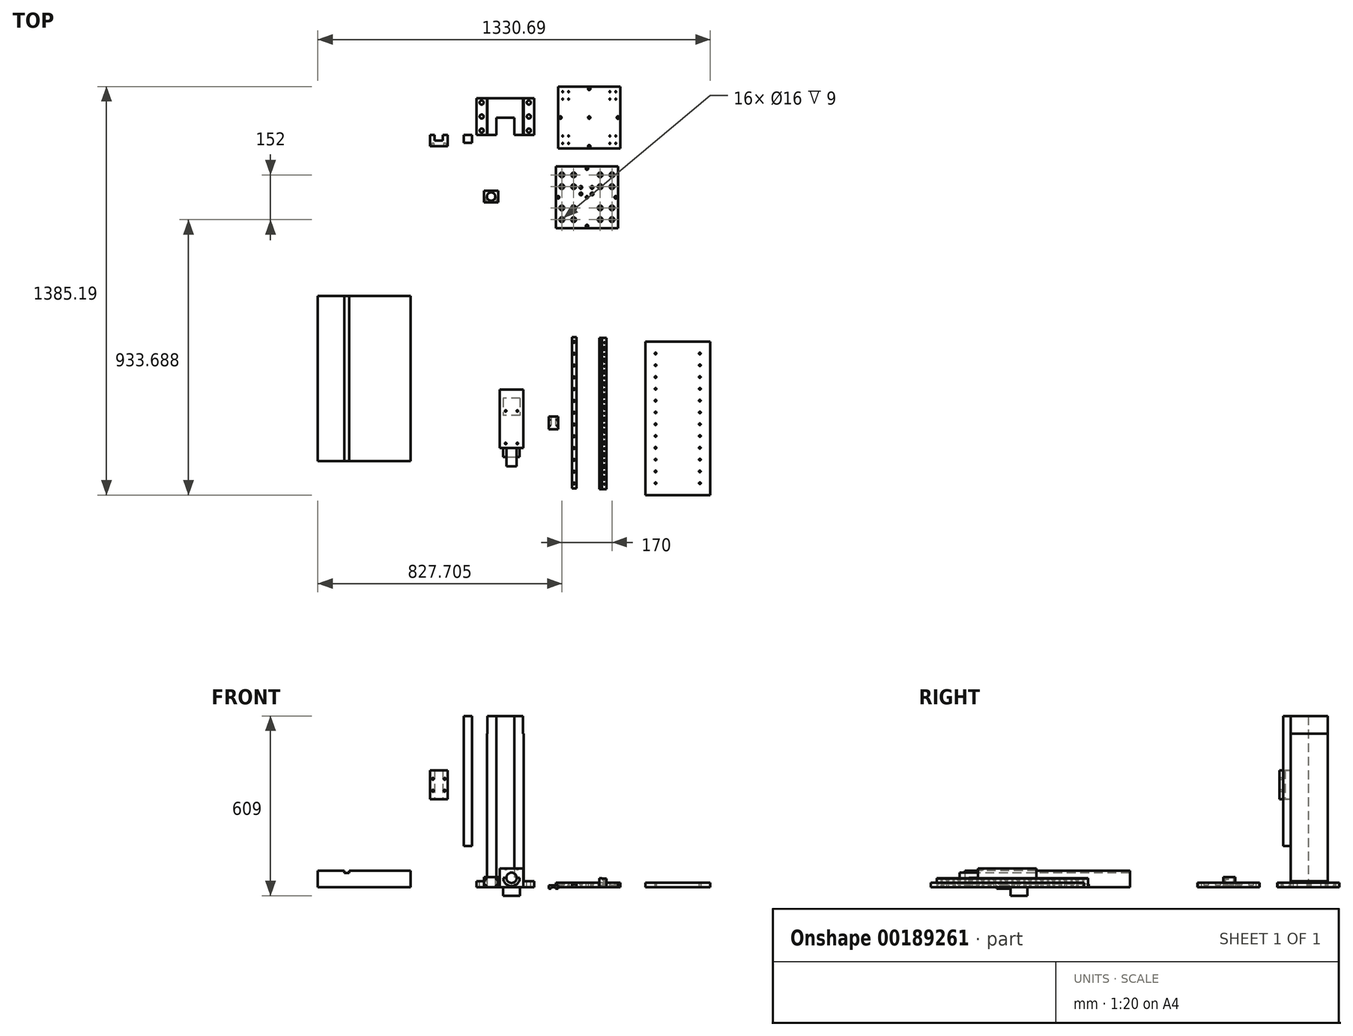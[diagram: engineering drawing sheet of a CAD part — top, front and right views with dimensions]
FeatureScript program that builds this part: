
annotation { "Feature Type Name" : "Feature", "Feature Type Description" : "" }
export const myFeature = defineFeature(function(context is Context, id is Id, definition is map)
    precondition{}
    {
        {
            var Q0;
            Q0=qCreatedBy(makeId("Top.planeOp"),FACE);
            var sketch = newSketch(context, id + "F0", { "sketchPlane" : qUnion([Q0])});
            skLineSegment(sketch, "E0.bottom", {"start": v(-121.15, 80.57) * mm, "end": v(3.85, 80.57) * mm});
            skLineSegment(sketch, "E0.top", {"start": v(-121.15, -44.43) * mm, "end": v(3.85, -44.43) * mm});
            skLineSegment(sketch, "E0.left", {"start": v(-121.15, 80.57) * mm, "end": v(-121.15, -44.43) * mm});
            skLineSegment(sketch, "E0.right", {"start": v(3.85, 80.57) * mm, "end": v(3.85, -44.43) * mm});
            skSolve(sketch);
        }
        {
            var Q0;
            Q0=makeQuery(id+"F0.imprint","IMPRINT",FACE,{"disambiguationData":[TD([[makeQuery(id+"F0.imprint","IMPRINT",EDGE,{"derivedFrom":sQuery(id+"F0.wireOp",EDGE,"E0.bottom")}),-1.0]])]});
            extrude(context, id + "F1", {"entities" : qUnion([Q0]), "depth" : 580 * mm});
        }
        {
            var Q0;
            Q0=makeQuery(id+"F1.opExtrude","SWEPT_FACE",FACE,{"disambiguationData":[OSD([sQuery(id+"F0.wireOp",EDGE,"E0.left")])]});
            var sketch = newSketch(context, id + "F2", { "sketchPlane" : qUnion([Q0])});
            skLineSegment(sketch, "E1.bottom", {"start": v(-80.57, 0) * mm, "end": v(44.43, 0) * mm});
            skLineSegment(sketch, "E1.top", {"start": v(-80.57, 20) * mm, "end": v(44.43, 20) * mm});
            skLineSegment(sketch, "E1.left", {"start": v(-80.57, 0) * mm, "end": v(-80.57, 20) * mm});
            skLineSegment(sketch, "E1.right", {"start": v(44.43, 0) * mm, "end": v(44.43, 20) * mm});
            skSolve(sketch);
        }
        {
            var Q0;
            Q0=makeQuery(id+"F2.imprint","IMPRINT",FACE,{"disambiguationData":[TD([[makeQuery(id+"F2.imprint","IMPRINT",EDGE,{"derivedFrom":sQuery(id+"F2.wireOp",EDGE,"E1.bottom")}),1.0]])]});
            extrude(context, id + "F3", {"entities" : qUnion([Q0]), "operationType" : NewBodyOperationType.ADD, "depth" : 35 * mm});
        }
        {
            var Q0;
            Q0=makeQuery(id+"F1.opExtrude","SWEPT_FACE",FACE,{"disambiguationData":[OSD([sQuery(id+"F0.wireOp",EDGE,"E0.right")])]});
            var sketch = newSketch(context, id + "F4", { "sketchPlane" : qUnion([Q0])});
            skLineSegment(sketch, "E2.bottom", {"start": v(-44.43, 0) * mm, "end": v(80.57, 0) * mm});
            skLineSegment(sketch, "E2.top", {"start": v(-44.43, 20) * mm, "end": v(80.57, 20) * mm});
            skLineSegment(sketch, "E2.left", {"start": v(-44.43, 0) * mm, "end": v(-44.43, 20) * mm});
            skLineSegment(sketch, "E2.right", {"start": v(80.57, 0) * mm, "end": v(80.57, 20) * mm});
            skSolve(sketch);
        }
        {
            var Q0;
            Q0=makeQuery(id+"F4.imprint","IMPRINT",FACE,{"disambiguationData":[TD([[makeQuery(id+"F4.imprint","IMPRINT",EDGE,{"derivedFrom":sQuery(id+"F4.wireOp",EDGE,"E2.bottom")}),-1.0]])]});
            extrude(context, id + "F5", {"entities" : qUnion([Q0]), "operationType" : NewBodyOperationType.ADD, "depth" : 35 * mm});
        }
        {
            var Q0;
            Q0=makeQuery(id+"F5.opExtrude","SWEPT_FACE",FACE,{"disambiguationData":[OSD([sQuery(id+"F4.wireOp",EDGE,"E2.top")])]});
            var sketch = newSketch(context, id + "F6", { "sketchPlane" : qUnion([Q0])});
            skCircle(sketch, "E3", {"center": v(21.35, 65.57) * mm, "radius": 7 * mm});
            skCircle(sketch, "E4", {"center": v(21.35, 18.07) * mm, "radius": 7 * mm});
            skCircle(sketch, "E5", {"center": v(21.35, -29.43) * mm, "radius": 7 * mm});
            skPoint(sketch, "E6", {"position": v(38.85, 18.07) * mm});
            skPoint(sketch, "E7", {"position": v(21.35, 80.57) * mm});
            skSolve(sketch);
        }
        {
            var Q0;
            Q0=makeQuery(id+"F6.imprint","IMPRINT",FACE,{"disambiguationData":[TD([[makeQuery(id+"F6.imprint","IMPRINT",EDGE,{"derivedFrom":sQuery(id+"F6.wireOp",EDGE,"E4")}),1.0]])]});
            var Q1;
            Q1=makeQuery(id+"F6.imprint","IMPRINT",FACE,{"disambiguationData":[TD([[makeQuery(id+"F6.imprint","IMPRINT",EDGE,{"derivedFrom":sQuery(id+"F6.wireOp",EDGE,"E5")}),1.0]])]});
            var Q2;
            Q2=makeQuery(id+"F6.imprint","IMPRINT",FACE,{"disambiguationData":[TD([[makeQuery(id+"F6.imprint","IMPRINT",EDGE,{"derivedFrom":sQuery(id+"F6.wireOp",EDGE,"E3")}),1.0]])]});
            extrude(context, id + "F7", {"entities" : qUnion([Q0, Q1, Q2]), "operationType" : NewBodyOperationType.REMOVE, "oppositeDirection" : true, "depth" : 20 * mm});
        }
        {
            var Q0;
            Q0=makeQuery(id+"F3.opExtrude","SWEPT_FACE",FACE,{"disambiguationData":[OSD([sQuery(id+"F2.wireOp",EDGE,"E1.top")])]});
            var sketch = newSketch(context, id + "F8", { "sketchPlane" : qUnion([Q0])});
            skPoint(sketch, "E8", {"position": v(-138.65, 80.57) * mm});
            skPoint(sketch, "E9", {"position": v(-156.15, 18.07) * mm});
            skCircle(sketch, "E10", {"center": v(-138.65, 65.57) * mm, "radius": 7 * mm});
            skCircle(sketch, "E11", {"center": v(-138.65, 18.07) * mm, "radius": 7 * mm});
            skCircle(sketch, "E12", {"center": v(-138.65, -29.43) * mm, "radius": 7 * mm});
            skSolve(sketch);
        }
        {
            var Q0;
            Q0=makeQuery(id+"F8.imprint","IMPRINT",FACE,{"disambiguationData":[TD([[makeQuery(id+"F8.imprint","IMPRINT",EDGE,{"derivedFrom":sQuery(id+"F8.wireOp",EDGE,"E10")}),1.0]])]});
            var Q1;
            Q1=makeQuery(id+"F8.imprint","IMPRINT",FACE,{"disambiguationData":[TD([[makeQuery(id+"F8.imprint","IMPRINT",EDGE,{"derivedFrom":sQuery(id+"F8.wireOp",EDGE,"E11")}),1.0]])]});
            var Q2;
            Q2=makeQuery(id+"F8.imprint","IMPRINT",FACE,{"disambiguationData":[TD([[makeQuery(id+"F8.imprint","IMPRINT",EDGE,{"derivedFrom":sQuery(id+"F8.wireOp",EDGE,"E12")}),1.0]])]});
            extrude(context, id + "F9", {"entities" : qUnion([Q0, Q1, Q2]), "operationType" : NewBodyOperationType.REMOVE, "oppositeDirection" : true, "depth" : 20 * mm});
        }
        {
            var Q0;
            {var subQ2=sQuery(id+"F2.wireOp",EDGE,"E1.top");Q0=makeQuery(id+"F2.imprint","IMPRINT",FACE,{"disambiguationData":[TD([[makeQuery(id+"F2.imprint","IMPRINT",EDGE,{"derivedFrom":subQ2}),1.0]])]});}
            var sketch = newSketch(context, id + "F10", { "sketchPlane" : qUnion([Q0])});
            skLineSegment(sketch, "E13.bottom", {"start": v(44.43, 580) * mm, "end": v(-80.57, 580) * mm});
            skLineSegment(sketch, "E13.top", {"start": v(44.43, 520) * mm, "end": v(-80.57, 520) * mm});
            skLineSegment(sketch, "E13.left", {"start": v(44.43, 580) * mm, "end": v(44.43, 520) * mm});
            skLineSegment(sketch, "E13.right", {"start": v(-80.57, 580) * mm, "end": v(-80.57, 520) * mm});
            skSolve(sketch);
        }
        {
            var Q0;
            Q0=makeQuery(id+"F10.imprint","IMPRINT",FACE,{"disambiguationData":[TD([[makeQuery(id+"F10.imprint","IMPRINT",EDGE,{"derivedFrom":sQuery(id+"F10.wireOp",EDGE,"E13.bottom")}),-1.0]])]});
            extrude(context, id + "F11", {"entities" : qUnion([Q0]), "operationType" : NewBodyOperationType.REMOVE, "oppositeDirection" : true, "depth" : 2 * mm});
        }
        {
            var Q0;
            {var subQ3=sQuery(id+"F4.wireOp",EDGE,"E2.top");Q0=makeQuery(id+"F4.imprint","IMPRINT",FACE,{"disambiguationData":[TD([[makeQuery(id+"F4.imprint","IMPRINT",EDGE,{"derivedFrom":subQ3}),1.0]])]});}
            var sketch = newSketch(context, id + "F12", { "sketchPlane" : qUnion([Q0])});
            skLineSegment(sketch, "E14.bottom", {"start": v(-44.43, 580) * mm, "end": v(80.57, 580) * mm});
            skLineSegment(sketch, "E14.top", {"start": v(-44.43, 520) * mm, "end": v(80.57, 520) * mm});
            skLineSegment(sketch, "E14.left", {"start": v(-44.43, 580) * mm, "end": v(-44.43, 520) * mm});
            skLineSegment(sketch, "E14.right", {"start": v(80.57, 580) * mm, "end": v(80.57, 520) * mm});
            skLineSegment(sketch, "E15", {"start": v(14.57, 580) * mm, "end": v(14.57, 50.87) * mm});
            skSolve(sketch);
        }
        {
            var Q0;
            Q0=makeQuery(id+"F12.imprint","IMPRINT",FACE,{"disambiguationData":[TD([[makeQuery(id+"F12.imprint","IMPRINT",EDGE,{"derivedFrom":sQuery(id+"F12.wireOp",EDGE,"E14.bottom")}),1.0]])]});
            extrude(context, id + "F13", {"entities" : qUnion([Q0]), "operationType" : NewBodyOperationType.REMOVE, "oppositeDirection" : true, "depth" : 2 * mm});
        }
        {
            var Q0;
            Q0=makeQuery(id+"F5.boolean.opBoolean","MERGE",FACE,{"derivedFrom":[makeQuery(id+"F3.boolean.opBoolean","MERGE",FACE,{"derivedFrom":[makeQuery(id+"F1.opExtrude","SWEPT_FACE",FACE,{"disambiguationData":[OSD([sQuery(id+"F0.wireOp",EDGE,"E0.top")])]}),makeQuery(id+"F3.opExtrude","SWEPT_FACE",FACE,{"disambiguationData":[OSD([sQuery(id+"F2.wireOp",EDGE,"E1.right")])]})]}),makeQuery(id+"F5.opExtrude","SWEPT_FACE",FACE,{"disambiguationData":[OSD([sQuery(id+"F4.wireOp",EDGE,"E2.left")])]})]});
            var sketch = newSketch(context, id + "F14", { "sketchPlane" : qUnion([Q0])});
            skPoint(sketch, "E16", {"position": v(-58.65, 580) * mm});
            skLineSegment(sketch, "E17.bottom", {"start": v(-88.9, 580) * mm, "end": v(-28.4, 580) * mm});
            skLineSegment(sketch, "E17.top", {"start": v(-88.9, 0) * mm, "end": v(-28.4, 0) * mm});
            skLineSegment(sketch, "E17.left", {"start": v(-88.9, 580) * mm, "end": v(-88.9, 0) * mm});
            skLineSegment(sketch, "E17.right", {"start": v(-28.4, 580) * mm, "end": v(-28.4, 0) * mm});
            skSolve(sketch);
        }
        {
            var Q0;
            Q0=makeQuery(id+"F14.imprint","IMPRINT",FACE,{"disambiguationData":[TD([[makeQuery(id+"F14.imprint","IMPRINT",EDGE,{"derivedFrom":sQuery(id+"F14.wireOp",EDGE,"E17.bottom")}),-1.0]])]});
            extrude(context, id + "F15", {"entities" : qUnion([Q0]), "operationType" : NewBodyOperationType.REMOVE, "oppositeDirection" : true, "depth" : 59 * mm});
        }
        {
            var Q0;
            Q0=makeQuery(id+"F5.boolean.opBoolean","MERGE",FACE,{"derivedFrom":[makeQuery(id+"F3.boolean.opBoolean","MERGE",FACE,{"derivedFrom":[makeQuery(id+"F1.opExtrude","SWEPT_FACE",FACE,{"disambiguationData":[OSD([sQuery(id+"F0.wireOp",EDGE,"E0.top")])]}),makeQuery(id+"F3.opExtrude","SWEPT_FACE",FACE,{"disambiguationData":[OSD([sQuery(id+"F2.wireOp",EDGE,"E1.right")])]})]}),makeQuery(id+"F5.opExtrude","SWEPT_FACE",FACE,{"disambiguationData":[OSD([sQuery(id+"F4.wireOp",EDGE,"E2.left")])]})]});
            var sketch = newSketch(context, id + "F16", { "sketchPlane" : qUnion([Q0])});
            skLineSegment(sketch, "E18.bottom", {"start": v(-199.32, 580) * mm, "end": v(-171.32, 580) * mm});
            skLineSegment(sketch, "E18.top", {"start": v(-199.32, 140) * mm, "end": v(-171.32, 140) * mm});
            skLineSegment(sketch, "E18.left", {"start": v(-199.32, 580) * mm, "end": v(-199.32, 140) * mm});
            skLineSegment(sketch, "E18.right", {"start": v(-171.32, 580) * mm, "end": v(-171.32, 140) * mm});
            skPoint(sketch, "E19", {"position": v(-185.32, 580) * mm});
            skPoint(sketch, "E20", {"position": v(-122.53, 0) * mm});
            skLineSegment(sketch, "E21.bottom", {"start": v(-314.15, 396.2) * mm, "end": v(-254.15, 396.2) * mm});
            skLineSegment(sketch, "E21.top", {"start": v(-314.15, 298.2) * mm, "end": v(-254.15, 298.2) * mm});
            skLineSegment(sketch, "E21.left", {"start": v(-314.15, 396.2) * mm, "end": v(-314.15, 298.2) * mm});
            skLineSegment(sketch, "E21.right", {"start": v(-254.15, 396.2) * mm, "end": v(-254.15, 298.2) * mm});
            skPoint(sketch, "E22", {"position": v(-284.15, 298.2) * mm});
            skSolve(sketch);
        }
        {
            var Q0;
            Q0=makeQuery(id+"F16.imprint","IMPRINT",FACE,{"disambiguationData":[TD([[makeQuery(id+"F16.imprint","IMPRINT",EDGE,{"derivedFrom":sQuery(id+"F16.wireOp",EDGE,"E18.bottom")}),-1.0]])]});
            extrude(context, id + "F17", {"entities" : qUnion([Q0]), "depth" : 26 * mm});
        }
        {
            var Q0;
            Q0=makeQuery(id+"F16.imprint","IMPRINT",FACE,{"disambiguationData":[TD([[makeQuery(id+"F16.imprint","IMPRINT",EDGE,{"derivedFrom":sQuery(id+"F16.wireOp",EDGE,"E21.bottom")}),-1.0]])]});
            extrude(context, id + "F18", {"entities" : qUnion([Q0]), "depth" : 38 * mm});
        }
        {
            var Q0;
            Q0=makeQuery(id+"F18.opExtrude","SWEPT_FACE",FACE,{"disambiguationData":[OSD([sQuery(id+"F16.wireOp",EDGE,"E21.top")])]});
            var sketch = newSketch(context, id + "F19", { "sketchPlane" : qUnion([Q0])});
            skLineSegment(sketch, "E23.bottom", {"start": v(-298.15, 44.43) * mm, "end": v(-270.15, 44.43) * mm});
            skLineSegment(sketch, "E23.top", {"start": v(-298.15, 63.43) * mm, "end": v(-270.15, 63.43) * mm});
            skLineSegment(sketch, "E23.left", {"start": v(-298.15, 44.43) * mm, "end": v(-298.15, 63.43) * mm});
            skLineSegment(sketch, "E23.right", {"start": v(-270.15, 44.43) * mm, "end": v(-270.15, 63.43) * mm});
            skPoint(sketch, "E24", {"position": v(-284.15, 44.43) * mm});
            skSolve(sketch);
        }
        {
            var Q0;
            Q0=makeQuery(id+"F19.imprint","IMPRINT",FACE,{"disambiguationData":[TD([[makeQuery(id+"F19.imprint","IMPRINT",EDGE,{"derivedFrom":sQuery(id+"F19.wireOp",EDGE,"E23.bottom")}),1.0]])]});
            extrude(context, id + "F20", {"entities" : qUnion([Q0]), "operationType" : NewBodyOperationType.REMOVE, "oppositeDirection" : true, "depth" : 98 * mm});
        }
        {
            var Q0;
            Q0=makeQuery(id+"F18.opExtrude","CAP_FACE",FACE,{"disambiguationData":[OSD([sQuery(id+"F16.wireOp",EDGE,"E21.bottom"),sQuery(id+"F16.wireOp",EDGE,"E21.top"),sQuery(id+"F16.wireOp",EDGE,"E21.left"),sQuery(id+"F16.wireOp",EDGE,"E21.right")])],"isStart":false});
            var sketch = newSketch(context, id + "F21", { "sketchPlane" : qUnion([Q0])});
            skCircle(sketch, "E25", {"center": v(-304.15, 367.2) * mm, "radius": 3.35 * mm});
            skCircle(sketch, "E26", {"center": v(-304.15, 327.2) * mm, "radius": 3.35 * mm});
            skCircle(sketch, "E27", {"center": v(-264.15, 367.2) * mm, "radius": 3.35 * mm});
            skCircle(sketch, "E28", {"center": v(-264.15, 327.2) * mm, "radius": 3.35 * mm});
            skPoint(sketch, "E29", {"position": v(-284.15, 396.2) * mm});
            skLineSegment(sketch, "E30", {"start": v(-284.15, 396.2) * mm, "end": v(-284.15, 298.2) * mm});
            skPoint(sketch, "E31", {"position": v(-284.15, 347.2) * mm});
            skSolve(sketch);
        }
        {
            var Q0;
            Q0=makeQuery(id+"F21.imprint","IMPRINT",FACE,{"disambiguationData":[TD([[makeQuery(id+"F21.imprint","IMPRINT",EDGE,{"derivedFrom":sQuery(id+"F21.wireOp",EDGE,"E25")}),1.0]])]});
            var Q1;
            Q1=makeQuery(id+"F21.imprint","IMPRINT",FACE,{"disambiguationData":[TD([[makeQuery(id+"F21.imprint","IMPRINT",EDGE,{"derivedFrom":sQuery(id+"F21.wireOp",EDGE,"E26")}),1.0]])]});
            var Q2;
            Q2=makeQuery(id+"F21.imprint","IMPRINT",FACE,{"disambiguationData":[TD([[makeQuery(id+"F21.imprint","IMPRINT",EDGE,{"derivedFrom":sQuery(id+"F21.wireOp",EDGE,"E27")}),1.0]])]});
            var Q3;
            Q3=makeQuery(id+"F21.imprint","IMPRINT",FACE,{"disambiguationData":[TD([[makeQuery(id+"F21.imprint","IMPRINT",EDGE,{"derivedFrom":sQuery(id+"F21.wireOp",EDGE,"E28")}),1.0]])]});
            extrude(context, id + "F22", {"entities" : qUnion([Q0, Q1, Q2, Q3]), "operationType" : NewBodyOperationType.REMOVE, "oppositeDirection" : true, "depth" : 10 * mm});
        }
        {
            var Q0;
            Q0=qCreatedBy(makeId("Top.planeOp"),FACE);
            var sketch = newSketch(context, id + "F23", { "sketchPlane" : qUnion([Q0])});
            skLineSegment(sketch, "E32.bottom", {"start": v(120.9, 119.72) * mm, "end": v(330.9, 119.72) * mm});
            skLineSegment(sketch, "E32.top", {"start": v(120.9, -90.28) * mm, "end": v(330.9, -90.28) * mm});
            skLineSegment(sketch, "E32.left", {"start": v(120.9, 119.72) * mm, "end": v(120.9, -90.28) * mm});
            skLineSegment(sketch, "E32.right", {"start": v(330.9, 119.72) * mm, "end": v(330.9, -90.28) * mm});
            skCircle(sketch, "E33", {"center": v(225.9, 14.72) * mm, "radius": 4 * mm});
            skCircle(sketch, "E34", {"center": v(323.4, 14.72) * mm, "radius": 4.2 * mm});
            skCircle(sketch, "E35", {"center": v(225.9, 112.22) * mm, "radius": 4.2 * mm});
            skCircle(sketch, "E36", {"center": v(128.4, 14.72) * mm, "radius": 4.2 * mm});
            skCircle(sketch, "E37", {"center": v(225.9, -82.78) * mm, "radius": 4.2 * mm});
            skLineSegment(sketch, "E38.bottom", {"start": v(113.2, -150.78) * mm, "end": v(323.2, -150.78) * mm});
            skLineSegment(sketch, "E38.top", {"start": v(113.2, -360.78) * mm, "end": v(323.2, -360.78) * mm});
            skLineSegment(sketch, "E38.left", {"start": v(113.2, -150.78) * mm, "end": v(113.2, -360.78) * mm});
            skLineSegment(sketch, "E38.right", {"start": v(323.2, -150.78) * mm, "end": v(323.2, -360.78) * mm});
            skCircle(sketch, "E39", {"center": v(218.2, -255.78) * mm, "radius": 4 * mm});
            skCircle(sketch, "E40", {"center": v(218.2, -158.28) * mm, "radius": 4.2 * mm});
            skCircle(sketch, "E41", {"center": v(120.7, -255.78) * mm, "radius": 4.2 * mm});
            skCircle(sketch, "E42", {"center": v(315.7, -255.78) * mm, "radius": 4.2 * mm});
            skCircle(sketch, "E43", {"center": v(218.2, -353.28) * mm, "radius": 4.2 * mm});
            skLineSegment(sketch, "E44.bottom", {"start": v(-694.5, -590.16) * mm, "end": v(-379.5, -590.16) * mm});
            skLineSegment(sketch, "E44.top", {"start": v(-694.5, -1150.16) * mm, "end": v(-379.5, -1150.16) * mm});
            skLineSegment(sketch, "E44.left", {"start": v(-694.5, -590.16) * mm, "end": v(-694.5, -1150.16) * mm});
            skLineSegment(sketch, "E44.right", {"start": v(-379.5, -590.16) * mm, "end": v(-379.5, -1150.16) * mm});
            skLineSegment(sketch, "E45.bottom", {"start": v(-130.67, -233.25) * mm, "end": v(-82.67, -233.25) * mm});
            skLineSegment(sketch, "E45.top", {"start": v(-130.67, -273.25) * mm, "end": v(-82.67, -273.25) * mm});
            skLineSegment(sketch, "E45.left", {"start": v(-130.67, -233.25) * mm, "end": v(-130.67, -273.25) * mm});
            skLineSegment(sketch, "E45.right", {"start": v(-82.67, -233.25) * mm, "end": v(-82.67, -273.25) * mm});
            skPoint(sketch, "E46", {"position": v(-106.67, -253.25) * mm});
            skCircle(sketch, "E47", {"center": v(-106.67, -253.25) * mm, "radius": 14 * mm});
            skCircle(sketch, "E48", {"center": v(303.2, -179.78) * mm, "radius": 4.5 * mm});
            skCircle(sketch, "E49", {"center": v(263.2, -179.78) * mm, "radius": 4.5 * mm});
            skCircle(sketch, "E50", {"center": v(263.2, -219.78) * mm, "radius": 4.5 * mm});
            skCircle(sketch, "E51", {"center": v(303.2, -219.78) * mm, "radius": 4.5 * mm});
            skCircle(sketch, "E52", {"center": v(303.2, -331.78) * mm, "radius": 4.5 * mm});
            skCircle(sketch, "E53", {"center": v(303.2, -291.78) * mm, "radius": 4.5 * mm});
            skCircle(sketch, "E54", {"center": v(263.2, -291.78) * mm, "radius": 4.5 * mm});
            skCircle(sketch, "E55", {"center": v(263.2, -331.78) * mm, "radius": 4.5 * mm});
            skCircle(sketch, "E56", {"center": v(173.2, -219.78) * mm, "radius": 4.5 * mm});
            skCircle(sketch, "E57", {"center": v(173.2, -179.78) * mm, "radius": 4.5 * mm});
            skCircle(sketch, "E58", {"center": v(133.2, -179.78) * mm, "radius": 4.5 * mm});
            skCircle(sketch, "E59", {"center": v(133.2, -219.78) * mm, "radius": 4.5 * mm});
            skCircle(sketch, "E60", {"center": v(173.2, -331.78) * mm, "radius": 4.5 * mm});
            skCircle(sketch, "E61", {"center": v(173.2, -291.78) * mm, "radius": 4.5 * mm});
            skCircle(sketch, "E62", {"center": v(133.2, -291.78) * mm, "radius": 4.5 * mm});
            skCircle(sketch, "E63", {"center": v(133.2, -331.78) * mm, "radius": 4.5 * mm});
            skCircle(sketch, "E64", {"center": v(263.2, -179.78) * mm, "radius": 8 * mm});
            skCircle(sketch, "E65", {"center": v(303.2, -179.78) * mm, "radius": 8 * mm});
            skCircle(sketch, "E66", {"center": v(263.2, -219.78) * mm, "radius": 8 * mm});
            skCircle(sketch, "E67", {"center": v(303.2, -219.78) * mm, "radius": 8 * mm});
            skCircle(sketch, "E68", {"center": v(263.2, -291.78) * mm, "radius": 8 * mm});
            skCircle(sketch, "E69", {"center": v(303.2, -291.78) * mm, "radius": 8 * mm});
            skCircle(sketch, "E70", {"center": v(263.2, -331.78) * mm, "radius": 8 * mm});
            skCircle(sketch, "E71", {"center": v(303.2, -331.78) * mm, "radius": 8 * mm});
            skCircle(sketch, "E72", {"center": v(173.2, -179.78) * mm, "radius": 8 * mm});
            skCircle(sketch, "E73", {"center": v(133.2, -179.78) * mm, "radius": 8 * mm});
            skCircle(sketch, "E74", {"center": v(133.2, -219.78) * mm, "radius": 8 * mm});
            skCircle(sketch, "E75", {"center": v(173.2, -219.78) * mm, "radius": 8 * mm});
            skCircle(sketch, "E76", {"center": v(133.2, -291.78) * mm, "radius": 8 * mm});
            skCircle(sketch, "E77", {"center": v(173.2, -291.78) * mm, "radius": 8 * mm});
            skCircle(sketch, "E78", {"center": v(133.2, -331.78) * mm, "radius": 8 * mm});
            skCircle(sketch, "E79", {"center": v(173.2, -331.78) * mm, "radius": 8 * mm});
            skCircle(sketch, "E80", {"center": v(197.7, -222.28) * mm, "radius": 2.65 * mm});
            skCircle(sketch, "E81", {"center": v(235.7, -222.28) * mm, "radius": 2.65 * mm});
            skCircle(sketch, "E82", {"center": v(197.7, -244.28) * mm, "radius": 2.65 * mm});
            skCircle(sketch, "E83", {"center": v(235.7, -244.28) * mm, "radius": 2.65 * mm});
            skCircle(sketch, "E84", {"center": v(197.7, -222.28) * mm, "radius": 4.75 * mm});
            skCircle(sketch, "E85", {"center": v(235.7, -222.28) * mm, "radius": 4.75 * mm});
            skCircle(sketch, "E86", {"center": v(197.7, -244.28) * mm, "radius": 4.75 * mm});
            skCircle(sketch, "E87", {"center": v(235.7, -244.28) * mm, "radius": 4.75 * mm});
            skLineSegment(sketch, "E88.bottom", {"start": v(-77.51, -907.41) * mm, "end": v(2.49, -907.41) * mm});
            skLineSegment(sketch, "E88.top", {"start": v(-77.51, -1105.61) * mm, "end": v(2.49, -1105.61) * mm});
            skLineSegment(sketch, "E88.left", {"start": v(-77.51, -907.41) * mm, "end": v(-77.51, -1105.61) * mm});
            skLineSegment(sketch, "E88.right", {"start": v(2.49, -907.41) * mm, "end": v(2.49, -1105.61) * mm});
            skCircle(sketch, "E89", {"center": v(-57.51, -1090.61) * mm, "radius": 2.68 * mm});
            skCircle(sketch, "E90", {"center": v(-17.51, -1090.61) * mm, "radius": 2.68 * mm});
            skCircle(sketch, "E91", {"center": v(-57.51, -980.61) * mm, "radius": 2.68 * mm});
            skCircle(sketch, "E92", {"center": v(-17.51, -980.61) * mm, "radius": 2.68 * mm});
            skLineSegment(sketch, "E93.bottom", {"start": v(88.31, -999.03) * mm, "end": v(120.31, -999.03) * mm});
            skLineSegment(sketch, "E93.top", {"start": v(88.31, -1042.03) * mm, "end": v(120.31, -1042.03) * mm});
            skLineSegment(sketch, "E93.left", {"start": v(88.31, -999.03) * mm, "end": v(88.31, -1042.03) * mm});
            skLineSegment(sketch, "E93.right", {"start": v(120.31, -999.03) * mm, "end": v(120.31, -1042.03) * mm});
            skLineSegment(sketch, "E94.bottom", {"start": v(167.32, -729.85) * mm, "end": v(182.32, -729.85) * mm});
            skLineSegment(sketch, "E94.top", {"start": v(167.32, -1242.85) * mm, "end": v(182.32, -1242.85) * mm});
            skLineSegment(sketch, "E94.left", {"start": v(167.32, -729.85) * mm, "end": v(167.32, -1242.85) * mm});
            skLineSegment(sketch, "E94.right", {"start": v(182.32, -729.85) * mm, "end": v(182.32, -1242.85) * mm});
            skCircle(sketch, "E95", {"center": v(174.82, -746.35) * mm, "radius": 1.75 * mm});
            skCircle(sketch, "E96", {"center": v(174.82, -786.35) * mm, "radius": 1.75 * mm});
            skCircle(sketch, "E97", {"center": v(174.82, -826.35) * mm, "radius": 1.75 * mm});
            skCircle(sketch, "E98", {"center": v(174.82, -866.35) * mm, "radius": 1.75 * mm});
            skCircle(sketch, "E99", {"center": v(174.82, -906.35) * mm, "radius": 1.75 * mm});
            skCircle(sketch, "E100", {"center": v(174.82, -946.35) * mm, "radius": 1.75 * mm});
            skCircle(sketch, "E101", {"center": v(174.82, -986.35) * mm, "radius": 1.75 * mm});
            skCircle(sketch, "E102", {"center": v(174.82, -1026.35) * mm, "radius": 1.75 * mm});
            skCircle(sketch, "E103", {"center": v(174.82, -1066.35) * mm, "radius": 1.75 * mm});
            skCircle(sketch, "E104", {"center": v(174.82, -1106.35) * mm, "radius": 1.75 * mm});
            skCircle(sketch, "E105", {"center": v(174.82, -1146.35) * mm, "radius": 1.75 * mm});
            skCircle(sketch, "E106", {"center": v(174.82, -1186.35) * mm, "radius": 1.75 * mm});
            skCircle(sketch, "E107", {"center": v(174.82, -1226.35) * mm, "radius": 1.75 * mm});
            skPoint(sketch, "E108", {"position": v(174.82, -729.85) * mm});
            skPoint(sketch, "E109", {"position": v(277.23, -732.27) * mm});
            skLineSegment(sketch, "E110.right", {"start": v(284.73, -732.27) * mm, "end": v(284.73, -1245.27) * mm});
            skLineSegment(sketch, "E110.left", {"start": v(269.73, -732.27) * mm, "end": v(269.73, -1245.27) * mm});
            skCircle(sketch, "E111", {"center": v(277.23, -948.77) * mm, "radius": 1.75 * mm});
            skCircle(sketch, "E112", {"center": v(277.23, -1228.77) * mm, "radius": 1.75 * mm});
            skCircle(sketch, "E113", {"center": v(277.23, -1068.77) * mm, "radius": 1.75 * mm});
            skCircle(sketch, "E114", {"center": v(277.23, -1108.77) * mm, "radius": 1.75 * mm});
            skCircle(sketch, "E115", {"center": v(277.23, -1148.77) * mm, "radius": 1.75 * mm});
            skCircle(sketch, "E116", {"center": v(277.23, -988.77) * mm, "radius": 1.75 * mm});
            skCircle(sketch, "E117", {"center": v(277.23, -908.77) * mm, "radius": 1.75 * mm});
            skCircle(sketch, "E118", {"center": v(277.23, -788.77) * mm, "radius": 1.75 * mm});
            skLineSegment(sketch, "E110.top", {"start": v(269.73, -1245.27) * mm, "end": v(284.73, -1245.27) * mm});
            skCircle(sketch, "E119", {"center": v(277.23, -868.77) * mm, "radius": 1.75 * mm});
            skCircle(sketch, "E120", {"center": v(277.23, -1188.77) * mm, "radius": 1.75 * mm});
            skCircle(sketch, "E121", {"center": v(277.23, -1028.77) * mm, "radius": 1.75 * mm});
            skCircle(sketch, "E122", {"center": v(277.23, -748.77) * mm, "radius": 1.75 * mm});
            skCircle(sketch, "E123", {"center": v(277.23, -828.77) * mm, "radius": 1.75 * mm});
            skLineSegment(sketch, "E110.bottom", {"start": v(269.73, -732.27) * mm, "end": v(284.73, -732.27) * mm});
            skLineSegment(sketch, "E124.bottom", {"start": v(269.73, -732.27) * mm, "end": v(260.23, -732.27) * mm});
            skLineSegment(sketch, "E124.top", {"start": v(269.73, -1245.27) * mm, "end": v(260.23, -1245.27) * mm});
            skLineSegment(sketch, "E124.right", {"start": v(260.23, -732.27) * mm, "end": v(260.23, -1245.27) * mm});
            skCircle(sketch, "E125", {"center": v(277.23, -1208.77) * mm, "radius": 2.8 * mm});
            skCircle(sketch, "E126", {"center": v(277.23, -1168.77) * mm, "radius": 2.8 * mm});
            skCircle(sketch, "E127", {"center": v(277.23, -1128.77) * mm, "radius": 2.8 * mm});
            skCircle(sketch, "E128", {"center": v(277.23, -1088.77) * mm, "radius": 2.8 * mm});
            skCircle(sketch, "E129", {"center": v(277.23, -1048.77) * mm, "radius": 2.8 * mm});
            skCircle(sketch, "E130", {"center": v(277.23, -1008.77) * mm, "radius": 2.8 * mm});
            skCircle(sketch, "E131", {"center": v(277.23, -968.77) * mm, "radius": 2.8 * mm});
            skCircle(sketch, "E132", {"center": v(277.23, -928.77) * mm, "radius": 2.8 * mm});
            skCircle(sketch, "E133", {"center": v(277.23, -888.77) * mm, "radius": 2.8 * mm});
            skCircle(sketch, "E134", {"center": v(277.23, -848.77) * mm, "radius": 2.8 * mm});
            skCircle(sketch, "E135", {"center": v(277.23, -808.77) * mm, "radius": 2.8 * mm});
            skCircle(sketch, "E136", {"center": v(277.23, -768.77) * mm, "radius": 2.8 * mm});
            skLineSegment(sketch, "E137.bottom", {"start": v(416.18, -745.47) * mm, "end": v(636.18, -745.47) * mm});
            skLineSegment(sketch, "E137.top", {"start": v(416.18, -1265.47) * mm, "end": v(636.18, -1265.47) * mm});
            skLineSegment(sketch, "E137.left", {"start": v(416.18, -745.47) * mm, "end": v(416.18, -1265.47) * mm});
            skLineSegment(sketch, "E137.right", {"start": v(636.18, -745.47) * mm, "end": v(636.18, -1265.47) * mm});
            skCircle(sketch, "E138", {"center": v(451.18, -905.47) * mm, "radius": 2.8 * mm});
            skCircle(sketch, "E139", {"center": v(451.18, -865.47) * mm, "radius": 2.8 * mm});
            skCircle(sketch, "E140", {"center": v(451.18, -825.47) * mm, "radius": 2.8 * mm});
            skCircle(sketch, "E141", {"center": v(451.18, -785.47) * mm, "radius": 2.8 * mm});
            skCircle(sketch, "E142", {"center": v(451.18, -1065.47) * mm, "radius": 2.8 * mm});
            skCircle(sketch, "E143", {"center": v(451.18, -1105.47) * mm, "radius": 2.8 * mm});
            skCircle(sketch, "E144", {"center": v(451.18, -1145.47) * mm, "radius": 2.8 * mm});
            skCircle(sketch, "E145", {"center": v(451.18, -1185.47) * mm, "radius": 2.8 * mm});
            skCircle(sketch, "E146", {"center": v(451.18, -1225.47) * mm, "radius": 2.8 * mm});
            skCircle(sketch, "E147", {"center": v(451.18, -945.47) * mm, "radius": 2.8 * mm});
            skCircle(sketch, "E148", {"center": v(451.18, -985.47) * mm, "radius": 2.8 * mm});
            skCircle(sketch, "E149", {"center": v(451.18, -1025.47) * mm, "radius": 2.8 * mm});
            skCircle(sketch, "E150", {"center": v(601.18, -905.47) * mm, "radius": 2.8 * mm});
            skCircle(sketch, "E151", {"center": v(601.18, -865.47) * mm, "radius": 2.8 * mm});
            skCircle(sketch, "E152", {"center": v(601.18, -825.47) * mm, "radius": 2.8 * mm});
            skCircle(sketch, "E153", {"center": v(601.18, -785.47) * mm, "radius": 2.8 * mm});
            skCircle(sketch, "E154", {"center": v(601.18, -1065.47) * mm, "radius": 2.8 * mm});
            skCircle(sketch, "E155", {"center": v(601.18, -1105.47) * mm, "radius": 2.8 * mm});
            skCircle(sketch, "E156", {"center": v(601.18, -1145.47) * mm, "radius": 2.8 * mm});
            skCircle(sketch, "E157", {"center": v(601.18, -1185.47) * mm, "radius": 2.8 * mm});
            skCircle(sketch, "E158", {"center": v(601.18, -1225.47) * mm, "radius": 2.8 * mm});
            skCircle(sketch, "E159", {"center": v(601.18, -945.47) * mm, "radius": 2.8 * mm});
            skCircle(sketch, "E160", {"center": v(601.18, -985.47) * mm, "radius": 2.8 * mm});
            skCircle(sketch, "E161", {"center": v(601.18, -1025.47) * mm, "radius": 2.8 * mm});
            skPoint(sketch, "E162", {"position": v(526.18, -745.47) * mm});
            skCircle(sketch, "E163", {"center": v(135.9, 102.22) * mm, "radius": 1.6 * mm});
            skCircle(sketch, "E164", {"center": v(155.9, 102.22) * mm, "radius": 1.6 * mm});
            skCircle(sketch, "E165", {"center": v(135.9, 77.22) * mm, "radius": 1.6 * mm});
            skCircle(sketch, "E166", {"center": v(155.9, 77.22) * mm, "radius": 1.6 * mm});
            skCircle(sketch, "E167", {"center": v(155.9, 102.22) * mm, "radius": 3 * mm});
            skCircle(sketch, "E168", {"center": v(155.9, 77.22) * mm, "radius": 3 * mm});
            skCircle(sketch, "E169", {"center": v(135.9, 102.22) * mm, "radius": 3 * mm});
            skCircle(sketch, "E170", {"center": v(135.9, 77.22) * mm, "radius": 3 * mm});
            skCircle(sketch, "E171.1.0.0", {"center": v(295.9, 77.22) * mm, "radius": 1.6 * mm});
            skCircle(sketch, "E171.1.0.1", {"center": v(295.9, 102.22) * mm, "radius": 1.6 * mm});
            skCircle(sketch, "E171.1.0.2", {"center": v(295.9, 77.22) * mm, "radius": 3 * mm});
            skCircle(sketch, "E171.1.0.3", {"center": v(315.9, 102.22) * mm, "radius": 1.6 * mm});
            skCircle(sketch, "E171.1.0.4", {"center": v(315.9, 77.22) * mm, "radius": 3 * mm});
            skCircle(sketch, "E171.1.0.5", {"center": v(315.9, 77.22) * mm, "radius": 1.6 * mm});
            skCircle(sketch, "E171.1.0.6", {"center": v(315.9, 102.22) * mm, "radius": 3 * mm});
            skCircle(sketch, "E171.1.0.7", {"center": v(295.9, 102.22) * mm, "radius": 3 * mm});
            skLineSegment(sketch, "E171.direction1", {"start": v(155.9, 77.22) * mm, "end": v(315.9, 77.22) * mm, "construction": true});
            skLineSegment(sketch, "E172.1.0.0", {"start": v(155.9, -72.78) * mm, "end": v(315.9, -72.78) * mm, "construction": true});
            skCircle(sketch, "E172.1.0.1", {"center": v(135.9, -47.78) * mm, "radius": 1.6 * mm});
            skCircle(sketch, "E172.1.0.2", {"center": v(155.9, -47.78) * mm, "radius": 1.6 * mm});
            skCircle(sketch, "E172.1.0.3", {"center": v(315.9, -47.78) * mm, "radius": 3 * mm});
            skCircle(sketch, "E172.1.0.4", {"center": v(295.9, -72.78) * mm, "radius": 3 * mm});
            skCircle(sketch, "E172.1.0.5", {"center": v(295.9, -72.78) * mm, "radius": 1.6 * mm});
            skCircle(sketch, "E172.1.0.6", {"center": v(135.9, -72.78) * mm, "radius": 3 * mm});
            skCircle(sketch, "E172.1.0.7", {"center": v(315.9, -47.78) * mm, "radius": 1.6 * mm});
            skCircle(sketch, "E172.1.0.8", {"center": v(135.9, -47.78) * mm, "radius": 3 * mm});
            skCircle(sketch, "E172.1.0.9", {"center": v(135.9, -72.78) * mm, "radius": 1.6 * mm});
            skCircle(sketch, "E172.1.0.10", {"center": v(155.9, -47.78) * mm, "radius": 3 * mm});
            skCircle(sketch, "E172.1.0.11", {"center": v(315.9, -72.78) * mm, "radius": 3 * mm});
            skCircle(sketch, "E172.1.0.12", {"center": v(295.9, -47.78) * mm, "radius": 3 * mm});
            skCircle(sketch, "E172.1.0.13", {"center": v(295.9, -47.78) * mm, "radius": 1.6 * mm});
            skCircle(sketch, "E172.1.0.14", {"center": v(155.9, -72.78) * mm, "radius": 1.6 * mm});
            skCircle(sketch, "E172.1.0.15", {"center": v(315.9, -72.78) * mm, "radius": 1.6 * mm});
            skCircle(sketch, "E172.1.0.16", {"center": v(155.9, -72.78) * mm, "radius": 3 * mm});
            skLineSegment(sketch, "E172.direction1", {"start": v(155.9, 77.22) * mm, "end": v(155.9, -72.78) * mm, "construction": true});
            skSolve(sketch);
        }
        {
            var Q0;
            Q0=makeQuery(id+"F23.imprint","IMPRINT",FACE,{"disambiguationData":[TD([[makeQuery(id+"F23.imprint","IMPRINT",EDGE,{"derivedFrom":sQuery(id+"F23.wireOp",EDGE,"E32.bottom")}),-1.0]])]});
            extrude(context, id + "F24", {"entities" : qUnion([Q0]), "depth" : 15 * mm});
        }
        {
            var Q0;
            Q0=makeQuery(id+"F23.imprint","IMPRINT",FACE,{"disambiguationData":[TD([[makeQuery(id+"F23.imprint","IMPRINT",EDGE,{"derivedFrom":sQuery(id+"F23.wireOp",EDGE,"E38.bottom")}),-1.0]])]});
            extrude(context, id + "F25", {"entities" : qUnion([Q0]), "depth" : 15 * mm});
        }
        {
            var Q0;
            Q0=makeQuery(id+"F23.imprint","IMPRINT",FACE,{"disambiguationData":[TD([[makeQuery(id+"F23.imprint","IMPRINT",EDGE,{"derivedFrom":sQuery(id+"F23.wireOp",EDGE,"E44.bottom")}),-1.0]])]});
            extrude(context, id + "F27", {"entities" : qUnion([Q0]), "depth" : 55 * mm});
        }
        {
            var Q0;
            Q0=makeQuery(id+"F23.imprint","IMPRINT",FACE,{"disambiguationData":[TD([[makeQuery(id+"F23.imprint","IMPRINT",EDGE,{"derivedFrom":sQuery(id+"F23.wireOp",EDGE,"E45.bottom")}),-1.0]])]});
            extrude(context, id + "F28", {"entities" : qUnion([Q0]), "depth" : 34 * mm});
        }
        {
            var Q0;
            Q0=makeQuery(id+"F27.opExtrude","SWEPT_FACE",FACE,{"disambiguationData":[OSD([sQuery(id+"F23.wireOp",EDGE,"E44.top")])]});
            var sketch = newSketch(context, id + "F29", { "sketchPlane" : qUnion([Q0])});
            skLineSegment(sketch, "E173.bottom", {"start": v(-604.5, 55) * mm, "end": v(-588.5, 55) * mm});
            skLineSegment(sketch, "E173.top", {"start": v(-604.5, 47.5) * mm, "end": v(-588.5, 47.5) * mm});
            skLineSegment(sketch, "E173.left", {"start": v(-604.5, 55) * mm, "end": v(-604.5, 47.5) * mm});
            skLineSegment(sketch, "E173.right", {"start": v(-588.5, 55) * mm, "end": v(-588.5, 47.5) * mm});
            skSolve(sketch);
        }
        {
            var Q0;
            Q0=makeQuery(id+"F29.imprint","IMPRINT",FACE,{"disambiguationData":[TD([[makeQuery(id+"F29.imprint","IMPRINT",EDGE,{"derivedFrom":sQuery(id+"F29.wireOp",EDGE,"E173.bottom")}),-1.0]])]});
            extrude(context, id + "F30", {"entities" : qUnion([Q0]), "operationType" : NewBodyOperationType.REMOVE, "oppositeDirection" : true, "depth" : 560 * mm});
        }
        {
            var Q0;
            Q0=makeQuery(id+"F23.imprint","IMPRINT",FACE,{"disambiguationData":[TD([[makeQuery(id+"F23.imprint","IMPRINT",EDGE,{"derivedFrom":sQuery(id+"F23.wireOp",EDGE,"E55")}),-1.0]])]});
            var Q1;
            Q1=makeQuery(id+"F23.imprint","IMPRINT",FACE,{"disambiguationData":[TD([[makeQuery(id+"F23.imprint","IMPRINT",EDGE,{"derivedFrom":sQuery(id+"F23.wireOp",EDGE,"E54")}),-1.0]])]});
            var Q2;
            Q2=makeQuery(id+"F23.imprint","IMPRINT",FACE,{"disambiguationData":[TD([[makeQuery(id+"F23.imprint","IMPRINT",EDGE,{"derivedFrom":sQuery(id+"F23.wireOp",EDGE,"E53")}),-1.0]])]});
            var Q3;
            Q3=makeQuery(id+"F23.imprint","IMPRINT",FACE,{"disambiguationData":[TD([[makeQuery(id+"F23.imprint","IMPRINT",EDGE,{"derivedFrom":sQuery(id+"F23.wireOp",EDGE,"E52")}),-1.0]])]});
            var Q4;
            Q4=makeQuery(id+"F23.imprint","IMPRINT",FACE,{"disambiguationData":[TD([[makeQuery(id+"F23.imprint","IMPRINT",EDGE,{"derivedFrom":sQuery(id+"F23.wireOp",EDGE,"E50")}),-1.0]])]});
            var Q5;
            Q5=makeQuery(id+"F23.imprint","IMPRINT",FACE,{"disambiguationData":[TD([[makeQuery(id+"F23.imprint","IMPRINT",EDGE,{"derivedFrom":sQuery(id+"F23.wireOp",EDGE,"E51")}),-1.0]])]});
            var Q6;
            Q6=makeQuery(id+"F23.imprint","IMPRINT",FACE,{"disambiguationData":[TD([[makeQuery(id+"F23.imprint","IMPRINT",EDGE,{"derivedFrom":sQuery(id+"F23.wireOp",EDGE,"E49")}),-1.0]])]});
            var Q7;
            Q7=makeQuery(id+"F23.imprint","IMPRINT",FACE,{"disambiguationData":[TD([[makeQuery(id+"F23.imprint","IMPRINT",EDGE,{"derivedFrom":sQuery(id+"F23.wireOp",EDGE,"E48")}),-1.0]])]});
            var Q8;
            Q8=makeQuery(id+"F23.imprint","IMPRINT",FACE,{"disambiguationData":[TD([[makeQuery(id+"F23.imprint","IMPRINT",EDGE,{"derivedFrom":sQuery(id+"F23.wireOp",EDGE,"E58")}),-1.0]])]});
            var Q9;
            Q9=makeQuery(id+"F23.imprint","IMPRINT",FACE,{"disambiguationData":[TD([[makeQuery(id+"F23.imprint","IMPRINT",EDGE,{"derivedFrom":sQuery(id+"F23.wireOp",EDGE,"E57")}),-1.0]])]});
            var Q10;
            Q10=makeQuery(id+"F23.imprint","IMPRINT",FACE,{"disambiguationData":[TD([[makeQuery(id+"F23.imprint","IMPRINT",EDGE,{"derivedFrom":sQuery(id+"F23.wireOp",EDGE,"E59")}),-1.0]])]});
            var Q11;
            Q11=makeQuery(id+"F23.imprint","IMPRINT",FACE,{"disambiguationData":[TD([[makeQuery(id+"F23.imprint","IMPRINT",EDGE,{"derivedFrom":sQuery(id+"F23.wireOp",EDGE,"E56")}),-1.0]])]});
            var Q12;
            Q12=makeQuery(id+"F23.imprint","IMPRINT",FACE,{"disambiguationData":[TD([[makeQuery(id+"F23.imprint","IMPRINT",EDGE,{"derivedFrom":sQuery(id+"F23.wireOp",EDGE,"E62")}),-1.0]])]});
            var Q13;
            Q13=makeQuery(id+"F23.imprint","IMPRINT",FACE,{"disambiguationData":[TD([[makeQuery(id+"F23.imprint","IMPRINT",EDGE,{"derivedFrom":sQuery(id+"F23.wireOp",EDGE,"E61")}),-1.0]])]});
            var Q14;
            Q14=makeQuery(id+"F23.imprint","IMPRINT",FACE,{"disambiguationData":[TD([[makeQuery(id+"F23.imprint","IMPRINT",EDGE,{"derivedFrom":sQuery(id+"F23.wireOp",EDGE,"E63")}),-1.0]])]});
            var Q15;
            Q15=makeQuery(id+"F23.imprint","IMPRINT",FACE,{"disambiguationData":[TD([[makeQuery(id+"F23.imprint","IMPRINT",EDGE,{"derivedFrom":sQuery(id+"F23.wireOp",EDGE,"E60")}),-1.0]])]});
            var Q16;
            Q16=sQuery(id+"F23.wireOp",EDGE,"E70");
            var Q17;
            Q17=sQuery(id+"F23.wireOp",EDGE,"E71");
            var Q18;
            Q18=sQuery(id+"F23.wireOp",EDGE,"E68");
            var Q19;
            Q19=sQuery(id+"F23.wireOp",EDGE,"E69");
            var Q20;
            Q20=sQuery(id+"F23.wireOp",EDGE,"E66");
            var Q21;
            Q21=sQuery(id+"F23.wireOp",EDGE,"E67");
            var Q22;
            Q22=sQuery(id+"F23.wireOp",EDGE,"E64");
            var Q23;
            Q23=sQuery(id+"F23.wireOp",EDGE,"E65");
            extrude(context, id + "F31", {"entities" : qUnion([Q0, Q1, Q2, Q3, Q4, Q5, Q6, Q7, Q8, Q9, Q10, Q11, Q12, Q13, Q14, Q15]), "operationType" : NewBodyOperationType.ADD, "surfaceEntities" : qUnion([Q16, Q17, Q18, Q19, Q20, Q21, Q22, Q23]), "depth" : 6 * mm});
        }
        {
            var Q0;
            Q0=makeQuery(id+"F28.opExtrude","SWEPT_FACE",FACE,{"disambiguationData":[OSD([sQuery(id+"F23.wireOp",EDGE,"E45.top")])]});
            var sketch = newSketch(context, id + "F32", { "sketchPlane" : qUnion([Q0])});
            skCircle(sketch, "E174", {"center": v(-125.67, 27.5) * mm, "radius": 2.02 * mm});
            skCircle(sketch, "E175", {"center": v(-87.67, 27.5) * mm, "radius": 2.02 * mm});
            skCircle(sketch, "E176", {"center": v(-125.67, 5.5) * mm, "radius": 2.02 * mm});
            skCircle(sketch, "E177", {"center": v(-87.67, 5.5) * mm, "radius": 2.02 * mm});
            skSolve(sketch);
        }
        {
            var Q0;
            Q0=makeQuery(id+"F32.imprint","IMPRINT",FACE,{"disambiguationData":[TD([[makeQuery(id+"F32.imprint","IMPRINT",EDGE,{"derivedFrom":sQuery(id+"F32.wireOp",EDGE,"E174")}),1.0]])]});
            var Q1;
            Q1=makeQuery(id+"F32.imprint","IMPRINT",FACE,{"disambiguationData":[TD([[makeQuery(id+"F32.imprint","IMPRINT",EDGE,{"derivedFrom":sQuery(id+"F32.wireOp",EDGE,"E176")}),1.0]])]});
            var Q2;
            Q2=makeQuery(id+"F32.imprint","IMPRINT",FACE,{"disambiguationData":[TD([[makeQuery(id+"F32.imprint","IMPRINT",EDGE,{"derivedFrom":sQuery(id+"F32.wireOp",EDGE,"E177")}),1.0]])]});
            var Q3;
            Q3=makeQuery(id+"F32.imprint","IMPRINT",FACE,{"disambiguationData":[TD([[makeQuery(id+"F32.imprint","IMPRINT",EDGE,{"derivedFrom":sQuery(id+"F32.wireOp",EDGE,"E175")}),1.0]])]});
            extrude(context, id + "F33", {"entities" : qUnion([Q0, Q1, Q2, Q3]), "operationType" : NewBodyOperationType.REMOVE, "oppositeDirection" : true, "depth" : 17 * mm});
        }
        {
            var Q0;
            Q0=makeQuery(id+"F23.imprint","IMPRINT",FACE,{"disambiguationData":[TD([[makeQuery(id+"F23.imprint","IMPRINT",EDGE,{"derivedFrom":sQuery(id+"F23.wireOp",EDGE,"E80")}),-1.0]])]});
            var Q1;
            Q1=makeQuery(id+"F23.imprint","IMPRINT",FACE,{"disambiguationData":[TD([[makeQuery(id+"F23.imprint","IMPRINT",EDGE,{"derivedFrom":sQuery(id+"F23.wireOp",EDGE,"E82")}),-1.0]])]});
            var Q2;
            Q2=makeQuery(id+"F23.imprint","IMPRINT",FACE,{"disambiguationData":[TD([[makeQuery(id+"F23.imprint","IMPRINT",EDGE,{"derivedFrom":sQuery(id+"F23.wireOp",EDGE,"E81")}),-1.0]])]});
            var Q3;
            Q3=makeQuery(id+"F23.imprint","IMPRINT",FACE,{"disambiguationData":[TD([[makeQuery(id+"F23.imprint","IMPRINT",EDGE,{"derivedFrom":sQuery(id+"F23.wireOp",EDGE,"E83")}),-1.0]])]});
            extrude(context, id + "F34", {"entities" : qUnion([Q0, Q1, Q2, Q3]), "operationType" : NewBodyOperationType.ADD, "depth" : 8 * mm});
        }
        {
            var Q0;
            Q0=makeQuery(id+"F23.imprint","IMPRINT",FACE,{"disambiguationData":[TD([[makeQuery(id+"F23.imprint","IMPRINT",EDGE,{"derivedFrom":sQuery(id+"F23.wireOp",EDGE,"E88.bottom")}),-1.0]])]});
            extrude(context, id + "F35", {"entities" : qUnion([Q0]), "depth" : 63 * mm});
        }
        {
            var Q0;
            Q0=makeQuery(id+"F23.imprint","IMPRINT",FACE,{"disambiguationData":[TD([[makeQuery(id+"F23.imprint","IMPRINT",EDGE,{"derivedFrom":sQuery(id+"F23.wireOp",EDGE,"E90")}),1.0]])]});
            var Q1;
            Q1=makeQuery(id+"F23.imprint","IMPRINT",FACE,{"disambiguationData":[TD([[makeQuery(id+"F23.imprint","IMPRINT",EDGE,{"derivedFrom":sQuery(id+"F23.wireOp",EDGE,"E89")}),1.0]])]});
            var Q2;
            Q2=makeQuery(id+"F23.imprint","IMPRINT",FACE,{"disambiguationData":[TD([[makeQuery(id+"F23.imprint","IMPRINT",EDGE,{"derivedFrom":sQuery(id+"F23.wireOp",EDGE,"E92")}),1.0]])]});
            var Q3;
            Q3=makeQuery(id+"F23.imprint","IMPRINT",FACE,{"disambiguationData":[TD([[makeQuery(id+"F23.imprint","IMPRINT",EDGE,{"derivedFrom":sQuery(id+"F23.wireOp",EDGE,"E91")}),1.0]])]});
            extrude(context, id + "F36", {"entities" : qUnion([Q0, Q1, Q2, Q3]), "operationType" : NewBodyOperationType.ADD, "depth" : 58 * mm});
        }
        {
            var Q0;
            Q0=makeQuery(id+"F23.imprint","IMPRINT",FACE,{"disambiguationData":[TD([[makeQuery(id+"F23.imprint","IMPRINT",EDGE,{"derivedFrom":sQuery(id+"F23.wireOp",EDGE,"E88.bottom")}),-1.0]])]});
            var sketch = newSketch(context, id + "F37", { "sketchPlane" : qUnion([Q0])});
            skLineSegment(sketch, "E178.bottom", {"start": v(-8.76, -937.61) * mm, "end": v(-66.26, -937.61) * mm});
            skLineSegment(sketch, "E178.top", {"start": v(-8.76, -995.11) * mm, "end": v(-66.26, -995.11) * mm});
            skLineSegment(sketch, "E178.left", {"start": v(-8.76, -937.61) * mm, "end": v(-8.76, -995.11) * mm});
            skLineSegment(sketch, "E178.right", {"start": v(-66.26, -937.61) * mm, "end": v(-66.26, -995.11) * mm});
            skSolve(sketch);
        }
        {
            var Q0;
            Q0=makeQuery(id+"F37.imprint","IMPRINT",FACE,{"disambiguationData":[TD([[makeQuery(id+"F37.imprint","IMPRINT",EDGE,{"derivedFrom":sQuery(id+"F37.wireOp",EDGE,"E178.bottom")}),1.0]])]});
            extrude(context, id + "F38", {"entities" : qUnion([Q0]), "operationType" : NewBodyOperationType.ADD, "oppositeDirection" : true, "depth" : 29 * mm});
        }
        {
            var Q0;
            Q0=makeQuery(id+"F23.imprint","IMPRINT",FACE,{"disambiguationData":[TD([[makeQuery(id+"F23.imprint","IMPRINT",EDGE,{"derivedFrom":sQuery(id+"F23.wireOp",EDGE,"E91")}),1.0]])]});
            var Q1;
            Q1=makeQuery(id+"F23.imprint","IMPRINT",FACE,{"disambiguationData":[TD([[makeQuery(id+"F23.imprint","IMPRINT",EDGE,{"derivedFrom":sQuery(id+"F23.wireOp",EDGE,"E92")}),1.0]])]});
            extrude(context, id + "F39", {"entities" : qUnion([Q0, Q1]), "operationType" : NewBodyOperationType.ADD, "oppositeDirection" : true, "depth" : 29 * mm});
        }
        {
            var Q0;
            Q0=makeQuery(id+"F35.opExtrude","SWEPT_FACE",FACE,{"disambiguationData":[OSD([sQuery(id+"F23.wireOp",EDGE,"E88.top")])]});
            var sketch = newSketch(context, id + "F40", { "sketchPlane" : qUnion([Q0])});
            skCircle(sketch, "E179", {"center": v(-37.51, 31.5) * mm, "radius": 28 * mm});
            skPoint(sketch, "E180", {"position": v(-77.51, 31.5) * mm});
            skPoint(sketch, "E181", {"position": v(-37.51, 63) * mm});
            skLineSegment(sketch, "E182", {"start": v(-77.51, 31.5) * mm, "end": v(2.49, 31.5) * mm});
            skLineSegment(sketch, "E183", {"start": v(-37.51, 63) * mm, "end": v(-37.51, 0) * mm});
            skCircle(sketch, "E184", {"center": v(-37.51, 31.5) * mm, "radius": 17.5 * mm});
            skSolve(sketch);
        }
        {
            var Q0;
            {var subQ0=sQuery(id+"F40.wireOp",EDGE,"E184");var subQ3=sQuery(id+"F40.wireOp",EDGE,"E182");var subQ4=makeQuery(id+"F40.imprint","INTERSECT",VERTEX,{"disambiguationData":[OD(0.0)],"derivedFrom":[subQ3,subQ0]});Q0=makeQuery(id+"F40.imprint","IMPRINT",FACE,{"disambiguationData":[TD([[makeQuery(id+"F40.imprint","IMPRINT",EDGE,{"disambiguationData":[TD([[subQ4,-1.0]])],"derivedFrom":subQ3}),1.0]])]});}
            var Q1;
            {var subQ1=sQuery(id+"F40.wireOp",EDGE,"E183");var subQ3=sQuery(id+"F40.wireOp",EDGE,"E182");var subQ5=makeQuery(id+"F40.imprint","INTERSECT",VERTEX,{"derivedFrom":[subQ3,subQ1]});Q1=makeQuery(id+"F40.imprint","IMPRINT",FACE,{"disambiguationData":[TD([[makeQuery(id+"F40.imprint","IMPRINT",EDGE,{"disambiguationData":[TD([[subQ5,-1.0]])],"derivedFrom":subQ3}),1.0]])]});}
            var Q2;
            {var subQ0=sQuery(id+"F40.wireOp",EDGE,"E184");var subQ3=sQuery(id+"F40.wireOp",EDGE,"E182");var subQ4=makeQuery(id+"F40.imprint","INTERSECT",VERTEX,{"disambiguationData":[OD(0.0)],"derivedFrom":[subQ3,subQ0]});Q2=makeQuery(id+"F40.imprint","IMPRINT",FACE,{"disambiguationData":[TD([[makeQuery(id+"F40.imprint","IMPRINT",EDGE,{"disambiguationData":[TD([[subQ4,-1.0]])],"derivedFrom":subQ3}),-1.0]])]});}
            var Q3;
            {var subQ0=sQuery(id+"F40.wireOp",EDGE,"E183");var subQ3=sQuery(id+"F40.wireOp",EDGE,"E182");var subQ4=makeQuery(id+"F40.imprint","INTERSECT",VERTEX,{"derivedFrom":[subQ3,subQ0]});Q3=makeQuery(id+"F40.imprint","IMPRINT",FACE,{"disambiguationData":[TD([[makeQuery(id+"F40.imprint","IMPRINT",EDGE,{"disambiguationData":[TD([[subQ4,-1.0]])],"derivedFrom":subQ3}),-1.0]])]});}
            extrude(context, id + "F41", {"entities" : qUnion([Q0, Q1, Q2, Q3]), "operationType" : NewBodyOperationType.ADD, "depth" : 62.5 * mm});
        }
        {
            var Q0;
            {var subQ3=sQuery(id+"F40.wireOp",EDGE,"E182");var subQ5=sQuery(id+"F40.wireOp",EDGE,"E179");var subQ7=makeQuery(id+"F40.imprint","INTERSECT",VERTEX,{"disambiguationData":[OD(1.0)],"derivedFrom":[subQ5,subQ3]});Q0=makeQuery(id+"F40.imprint","IMPRINT",FACE,{"disambiguationData":[TD([[makeQuery(id+"F40.imprint","IMPRINT",EDGE,{"disambiguationData":[TD([[subQ7,-1.0]])],"derivedFrom":subQ5}),1.0]])]});}
            var Q1;
            {var subQ0=sQuery(id+"F40.wireOp",EDGE,"E183");var subQ3=sQuery(id+"F40.wireOp",EDGE,"E179");var subQ4=makeQuery(id+"F40.imprint","INTERSECT",VERTEX,{"disambiguationData":[OD(0.0)],"derivedFrom":[subQ3,subQ0]});Q1=makeQuery(id+"F40.imprint","IMPRINT",FACE,{"disambiguationData":[TD([[makeQuery(id+"F40.imprint","IMPRINT",EDGE,{"disambiguationData":[TD([[subQ4,-1.0]])],"derivedFrom":subQ3}),1.0]])]});}
            var Q2;
            {var subQ1=sQuery(id+"F40.wireOp",EDGE,"E183");var subQ5=sQuery(id+"F40.wireOp",EDGE,"E179");var subQ6=makeQuery(id+"F40.imprint","INTERSECT",VERTEX,{"disambiguationData":[OD(0.0)],"derivedFrom":[subQ5,subQ1]});Q2=makeQuery(id+"F40.imprint","IMPRINT",FACE,{"disambiguationData":[TD([[makeQuery(id+"F40.imprint","IMPRINT",EDGE,{"disambiguationData":[TD([[subQ6,1.0]])],"derivedFrom":subQ5}),1.0]])]});}
            var Q3;
            {var subQ3=sQuery(id+"F40.wireOp",EDGE,"E182");var subQ5=sQuery(id+"F40.wireOp",EDGE,"E179");var subQ7=makeQuery(id+"F40.imprint","INTERSECT",VERTEX,{"disambiguationData":[OD(0.0)],"derivedFrom":[subQ5,subQ3]});Q3=makeQuery(id+"F40.imprint","IMPRINT",FACE,{"disambiguationData":[TD([[makeQuery(id+"F40.imprint","IMPRINT",EDGE,{"disambiguationData":[TD([[subQ7,1.0]])],"derivedFrom":subQ5}),1.0]])]});}
            extrude(context, id + "F42", {"entities" : qUnion([Q0, Q1, Q2, Q3]), "operationType" : NewBodyOperationType.ADD, "depth" : 30.5 * mm});
        }
        {
            var Q0;
            Q0=makeQuery(id+"F23.imprint","IMPRINT",FACE,{"disambiguationData":[TD([[makeQuery(id+"F23.imprint","IMPRINT",EDGE,{"derivedFrom":sQuery(id+"F23.wireOp",EDGE,"E93.bottom")}),-1.0]])]});
            extrude(context, id + "F43", {"entities" : qUnion([Q0]), "depth" : 6.5 * mm});
        }
        {
            var Q0;
            Q0=makeQuery(id+"F23.imprint","IMPRINT",FACE,{"disambiguationData":[TD([[makeQuery(id+"F23.imprint","IMPRINT",EDGE,{"derivedFrom":sQuery(id+"F23.wireOp",EDGE,"E93.bottom")}),-1.0]])]});
            var sketch = newSketch(context, id + "F44", { "sketchPlane" : qUnion([Q0])});
            skLineSegment(sketch, "E185.bottom", {"start": v(120.31, -999.03) * mm, "end": v(111.81, -999.03) * mm});
            skLineSegment(sketch, "E185.top", {"start": v(120.31, -1042.03) * mm, "end": v(111.81, -1042.03) * mm});
            skLineSegment(sketch, "E185.left", {"start": v(120.31, -999.03) * mm, "end": v(120.31, -1042.03) * mm});
            skLineSegment(sketch, "E185.right", {"start": v(111.81, -999.03) * mm, "end": v(111.81, -1042.03) * mm});
            skLineSegment(sketch, "E186.bottom", {"start": v(96.81, -999.03) * mm, "end": v(88.31, -999.03) * mm});
            skLineSegment(sketch, "E186.top", {"start": v(96.81, -1042.03) * mm, "end": v(88.31, -1042.03) * mm});
            skLineSegment(sketch, "E186.left", {"start": v(96.81, -999.03) * mm, "end": v(96.81, -1042.03) * mm});
            skLineSegment(sketch, "E186.right", {"start": v(88.31, -999.03) * mm, "end": v(88.31, -1042.03) * mm});
            skSolve(sketch);
        }
        {
            var Q0;
            Q0=qSketchRegion(id+"F44",true);
            extrude(context, id + "F45", {"entities" : qUnion([Q0]), "operationType" : NewBodyOperationType.ADD, "oppositeDirection" : true, "depth" : 5.5 * mm});
        }
        {
            var Q0;
            Q0=makeQuery(id+"F43.opExtrude","CAP_FACE",FACE,{"disambiguationData":[OSD([sQuery(id+"F23.wireOp",EDGE,"E93.bottom"),sQuery(id+"F23.wireOp",EDGE,"E93.top"),sQuery(id+"F23.wireOp",EDGE,"E93.left"),sQuery(id+"F23.wireOp",EDGE,"E93.right")])],"isStart":false});
            var sketch = newSketch(context, id + "F46", { "sketchPlane" : qUnion([Q0])});
            skCircle(sketch, "E187", {"center": v(91.81, -1010.53) * mm, "radius": 1.34 * mm});
            skCircle(sketch, "E188", {"center": v(116.81, -1010.53) * mm, "radius": 1.34 * mm});
            skCircle(sketch, "E189", {"center": v(91.81, -1030.53) * mm, "radius": 1.34 * mm});
            skCircle(sketch, "E190", {"center": v(116.81, -1030.53) * mm, "radius": 1.34 * mm});
            skSolve(sketch);
        }
        {
            var Q0;
            Q0=makeQuery(id+"F46.imprint","IMPRINT",FACE,{"disambiguationData":[TD([[makeQuery(id+"F46.imprint","IMPRINT",EDGE,{"derivedFrom":sQuery(id+"F46.wireOp",EDGE,"E189")}),1.0]])]});
            var Q1;
            Q1=makeQuery(id+"F46.imprint","IMPRINT",FACE,{"disambiguationData":[TD([[makeQuery(id+"F46.imprint","IMPRINT",EDGE,{"derivedFrom":sQuery(id+"F46.wireOp",EDGE,"E187")}),1.0]])]});
            var Q2;
            Q2=makeQuery(id+"F46.imprint","IMPRINT",FACE,{"disambiguationData":[TD([[makeQuery(id+"F46.imprint","IMPRINT",EDGE,{"derivedFrom":sQuery(id+"F46.wireOp",EDGE,"E188")}),1.0]])]});
            var Q3;
            Q3=makeQuery(id+"F46.imprint","IMPRINT",FACE,{"disambiguationData":[TD([[makeQuery(id+"F46.imprint","IMPRINT",EDGE,{"derivedFrom":sQuery(id+"F46.wireOp",EDGE,"E190")}),1.0]])]});
            var Q4;
            Q4=sQuery(id+"F46.wireOp",EDGE,"E187");
            var Q5;
            Q5=sQuery(id+"F46.wireOp",EDGE,"E189");
            var Q6;
            Q6=sQuery(id+"F46.wireOp",EDGE,"E190");
            var Q7;
            Q7=sQuery(id+"F46.wireOp",EDGE,"E188");
            extrude(context, id + "F47", {"entities" : qUnion([Q0, Q1, Q2, Q3]), "operationType" : NewBodyOperationType.REMOVE, "surfaceEntities" : qUnion([Q4, Q5, Q6, Q7]), "oppositeDirection" : true, "depth" : 4 * mm});
        }
        {
            var Q0;
            Q0=makeQuery(id+"F23.imprint","IMPRINT",FACE,{"disambiguationData":[TD([[makeQuery(id+"F23.imprint","IMPRINT",EDGE,{"derivedFrom":sQuery(id+"F23.wireOp",EDGE,"E94.bottom")}),-1.0]])]});
            extrude(context, id + "F48", {"entities" : qUnion([Q0]), "depth" : 9.5 * mm});
        }
        {
            var Q0;
            Q0=makeQuery(id+"F48.opExtrude","CAP_FACE",FACE,{"disambiguationData":[OSD([sQuery(id+"F23.wireOp",EDGE,"E94.bottom"),sQuery(id+"F23.wireOp",EDGE,"E94.top"),sQuery(id+"F23.wireOp",EDGE,"E94.left"),sQuery(id+"F23.wireOp",EDGE,"E94.right"),sQuery(id+"F23.wireOp",EDGE,"E95"),sQuery(id+"F23.wireOp",EDGE,"E96"),sQuery(id+"F23.wireOp",EDGE,"E97"),sQuery(id+"F23.wireOp",EDGE,"E98"),sQuery(id+"F23.wireOp",EDGE,"E99"),sQuery(id+"F23.wireOp",EDGE,"E100"),sQuery(id+"F23.wireOp",EDGE,"E101"),sQuery(id+"F23.wireOp",EDGE,"E102"),sQuery(id+"F23.wireOp",EDGE,"E103"),sQuery(id+"F23.wireOp",EDGE,"E104"),sQuery(id+"F23.wireOp",EDGE,"E105"),sQuery(id+"F23.wireOp",EDGE,"E106"),sQuery(id+"F23.wireOp",EDGE,"E107")])],"isStart":false});
            var sketch = newSketch(context, id + "F49", { "sketchPlane" : qUnion([Q0])});
            skCircle(sketch, "E191", {"center": v(174.82, -746.35) * mm, "radius": 3 * mm});
            skCircle(sketch, "E192", {"center": v(174.82, -786.35) * mm, "radius": 3 * mm});
            skCircle(sketch, "E193", {"center": v(174.82, -826.35) * mm, "radius": 3 * mm});
            skCircle(sketch, "E194", {"center": v(174.82, -866.35) * mm, "radius": 3 * mm});
            skCircle(sketch, "E195", {"center": v(174.82, -906.35) * mm, "radius": 3 * mm});
            skCircle(sketch, "E196", {"center": v(174.82, -946.35) * mm, "radius": 3 * mm});
            skCircle(sketch, "E197", {"center": v(174.82, -986.35) * mm, "radius": 3 * mm});
            skCircle(sketch, "E198", {"center": v(174.82, -1026.35) * mm, "radius": 3 * mm});
            skCircle(sketch, "E199", {"center": v(174.82, -1066.35) * mm, "radius": 3 * mm});
            skCircle(sketch, "E200", {"center": v(174.82, -1106.35) * mm, "radius": 3 * mm});
            skCircle(sketch, "E201", {"center": v(174.82, -1146.35) * mm, "radius": 3 * mm});
            skCircle(sketch, "E202", {"center": v(174.82, -1186.35) * mm, "radius": 3 * mm});
            skCircle(sketch, "E203", {"center": v(174.82, -1226.35) * mm, "radius": 3 * mm});
            skSolve(sketch);
        }
        {
            var Q0;
            Q0=makeQuery(id+"F49.imprint","IMPRINT",FACE,{"disambiguationData":[TD([[makeQuery(id+"F49.imprint","IMPRINT",EDGE,{"derivedFrom":sQuery(id+"F49.wireOp",EDGE,"E191")}),1.0]])]});
            var Q1;
            Q1=makeQuery(id+"F49.imprint","IMPRINT",FACE,{"disambiguationData":[TD([[makeQuery(id+"F49.imprint","IMPRINT",EDGE,{"derivedFrom":sQuery(id+"F49.wireOp",EDGE,"E192")}),1.0]])]});
            var Q2;
            Q2=makeQuery(id+"F49.imprint","IMPRINT",FACE,{"disambiguationData":[TD([[makeQuery(id+"F49.imprint","IMPRINT",EDGE,{"derivedFrom":sQuery(id+"F49.wireOp",EDGE,"E193")}),1.0]])]});
            var Q3;
            Q3=makeQuery(id+"F49.imprint","IMPRINT",FACE,{"disambiguationData":[TD([[makeQuery(id+"F49.imprint","IMPRINT",EDGE,{"derivedFrom":sQuery(id+"F49.wireOp",EDGE,"E194")}),1.0]])]});
            var Q4;
            Q4=makeQuery(id+"F49.imprint","IMPRINT",FACE,{"disambiguationData":[TD([[makeQuery(id+"F49.imprint","IMPRINT",EDGE,{"derivedFrom":sQuery(id+"F49.wireOp",EDGE,"E195")}),1.0]])]});
            var Q5;
            Q5=makeQuery(id+"F49.imprint","IMPRINT",FACE,{"disambiguationData":[TD([[makeQuery(id+"F49.imprint","IMPRINT",EDGE,{"derivedFrom":sQuery(id+"F49.wireOp",EDGE,"E196")}),1.0]])]});
            var Q6;
            Q6=makeQuery(id+"F49.imprint","IMPRINT",FACE,{"disambiguationData":[TD([[makeQuery(id+"F49.imprint","IMPRINT",EDGE,{"derivedFrom":sQuery(id+"F49.wireOp",EDGE,"E197")}),1.0]])]});
            var Q7;
            Q7=makeQuery(id+"F49.imprint","IMPRINT",FACE,{"disambiguationData":[TD([[makeQuery(id+"F49.imprint","IMPRINT",EDGE,{"derivedFrom":sQuery(id+"F49.wireOp",EDGE,"E198")}),1.0]])]});
            var Q8;
            Q8=makeQuery(id+"F49.imprint","IMPRINT",FACE,{"disambiguationData":[TD([[makeQuery(id+"F49.imprint","IMPRINT",EDGE,{"derivedFrom":sQuery(id+"F49.wireOp",EDGE,"E199")}),1.0]])]});
            var Q9;
            Q9=makeQuery(id+"F49.imprint","IMPRINT",FACE,{"disambiguationData":[TD([[makeQuery(id+"F49.imprint","IMPRINT",EDGE,{"derivedFrom":sQuery(id+"F49.wireOp",EDGE,"E200")}),1.0]])]});
            var Q10;
            Q10=makeQuery(id+"F49.imprint","IMPRINT",FACE,{"disambiguationData":[TD([[makeQuery(id+"F49.imprint","IMPRINT",EDGE,{"derivedFrom":sQuery(id+"F49.wireOp",EDGE,"E201")}),1.0]])]});
            var Q11;
            Q11=makeQuery(id+"F49.imprint","IMPRINT",FACE,{"disambiguationData":[TD([[makeQuery(id+"F49.imprint","IMPRINT",EDGE,{"derivedFrom":sQuery(id+"F49.wireOp",EDGE,"E202")}),1.0]])]});
            var Q12;
            Q12=makeQuery(id+"F49.imprint","IMPRINT",FACE,{"disambiguationData":[TD([[makeQuery(id+"F49.imprint","IMPRINT",EDGE,{"derivedFrom":sQuery(id+"F49.wireOp",EDGE,"E203")}),1.0]])]});
            var Q13;
            Q13=sQuery(id+"F49.wireOp",EDGE,"E191");
            var Q14;
            Q14=sQuery(id+"F49.wireOp",EDGE,"E192");
            var Q15;
            Q15=sQuery(id+"F49.wireOp",EDGE,"E193");
            var Q16;
            Q16=sQuery(id+"F49.wireOp",EDGE,"E194");
            var Q17;
            Q17=sQuery(id+"F49.wireOp",EDGE,"E195");
            var Q18;
            Q18=sQuery(id+"F49.wireOp",EDGE,"E196");
            var Q19;
            Q19=sQuery(id+"F49.wireOp",EDGE,"E197");
            var Q20;
            Q20=sQuery(id+"F49.wireOp",EDGE,"E198");
            var Q21;
            Q21=sQuery(id+"F49.wireOp",EDGE,"E199");
            var Q22;
            Q22=sQuery(id+"F49.wireOp",EDGE,"E200");
            var Q23;
            Q23=sQuery(id+"F49.wireOp",EDGE,"E201");
            var Q24;
            Q24=sQuery(id+"F49.wireOp",EDGE,"E202");
            var Q25;
            Q25=sQuery(id+"F49.wireOp",EDGE,"E203");
            extrude(context, id + "F50", {"entities" : qUnion([Q0, Q1, Q2, Q3, Q4, Q5, Q6, Q7, Q8, Q9, Q10, Q11, Q12]), "operationType" : NewBodyOperationType.REMOVE, "surfaceEntities" : qUnion([Q13, Q14, Q15, Q16, Q17, Q18, Q19, Q20, Q21, Q22, Q23, Q24, Q25]), "oppositeDirection" : true, "depth" : 4.7 * mm});
        }
        {
            var Q0;
            Q0=makeQuery(id+"F23.imprint","IMPRINT",FACE,{"disambiguationData":[TD([[makeQuery(id+"F23.imprint","IMPRINT",EDGE,{"derivedFrom":sQuery(id+"F23.wireOp",EDGE,"E124.bottom")}),1.0]])]});
            extrude(context, id + "F51", {"entities" : qUnion([Q0]), "depth" : 30 * mm});
        }
        {
            var Q0;
            Q0=makeQuery(id+"F23.imprint","IMPRINT",FACE,{"disambiguationData":[TD([[makeQuery(id+"F23.imprint","IMPRINT",EDGE,{"derivedFrom":sQuery(id+"F23.wireOp",EDGE,"E110.right")}),-1.0]])]});
            extrude(context, id + "F52", {"entities" : qUnion([Q0]), "operationType" : NewBodyOperationType.ADD, "depth" : 29 * mm});
        }
        {
            var Q0;
            Q0=makeQuery(id+"F52.opExtrude","CAP_FACE",FACE,{"disambiguationData":[OSD([sQuery(id+"F23.wireOp",EDGE,"E110.right"),sQuery(id+"F23.wireOp",EDGE,"E111"),sQuery(id+"F23.wireOp",EDGE,"E112"),sQuery(id+"F23.wireOp",EDGE,"E113"),sQuery(id+"F23.wireOp",EDGE,"E114"),sQuery(id+"F23.wireOp",EDGE,"E115"),sQuery(id+"F23.wireOp",EDGE,"E116"),sQuery(id+"F23.wireOp",EDGE,"E117"),sQuery(id+"F23.wireOp",EDGE,"E118"),sQuery(id+"F23.wireOp",EDGE,"E110.top"),sQuery(id+"F23.wireOp",EDGE,"E119"),sQuery(id+"F23.wireOp",EDGE,"E120"),sQuery(id+"F23.wireOp",EDGE,"E121"),sQuery(id+"F23.wireOp",EDGE,"E122"),sQuery(id+"F23.wireOp",EDGE,"E123"),sQuery(id+"F23.wireOp",EDGE,"E110.bottom"),sQuery(id+"F23.wireOp",EDGE,"E110.left"),sQuery(id+"F23.wireOp",EDGE,"E125"),sQuery(id+"F23.wireOp",EDGE,"E126"),sQuery(id+"F23.wireOp",EDGE,"E127"),sQuery(id+"F23.wireOp",EDGE,"E128"),sQuery(id+"F23.wireOp",EDGE,"E129"),sQuery(id+"F23.wireOp",EDGE,"E130"),sQuery(id+"F23.wireOp",EDGE,"E131"),sQuery(id+"F23.wireOp",EDGE,"E132"),sQuery(id+"F23.wireOp",EDGE,"E133"),sQuery(id+"F23.wireOp",EDGE,"E134"),sQuery(id+"F23.wireOp",EDGE,"E135"),sQuery(id+"F23.wireOp",EDGE,"E136")])],"isStart":false});
            var sketch = newSketch(context, id + "F53", { "sketchPlane" : qUnion([Q0])});
            skCircle(sketch, "E204", {"center": v(277.23, -768.77) * mm, "radius": 5 * mm});
            skCircle(sketch, "E205", {"center": v(277.23, -808.77) * mm, "radius": 5 * mm});
            skCircle(sketch, "E206", {"center": v(277.23, -848.77) * mm, "radius": 5 * mm});
            skCircle(sketch, "E207", {"center": v(277.23, -888.77) * mm, "radius": 5 * mm});
            skCircle(sketch, "E208", {"center": v(277.23, -928.77) * mm, "radius": 5 * mm});
            skCircle(sketch, "E209", {"center": v(277.23, -968.77) * mm, "radius": 5 * mm});
            skCircle(sketch, "E210", {"center": v(277.23, -1008.77) * mm, "radius": 5 * mm});
            skCircle(sketch, "E211", {"center": v(277.23, -1048.77) * mm, "radius": 5 * mm});
            skCircle(sketch, "E212", {"center": v(277.23, -1088.77) * mm, "radius": 5 * mm});
            skCircle(sketch, "E213", {"center": v(277.23, -1128.77) * mm, "radius": 5 * mm});
            skCircle(sketch, "E214", {"center": v(277.23, -1168.77) * mm, "radius": 5 * mm});
            skCircle(sketch, "E215", {"center": v(277.23, -1208.77) * mm, "radius": 5 * mm});
            skSolve(sketch);
        }
        {
            var Q0;
            Q0=makeQuery(id+"F53.imprint","IMPRINT",FACE,{"disambiguationData":[TD([[makeQuery(id+"F53.imprint","IMPRINT",EDGE,{"derivedFrom":sQuery(id+"F53.wireOp",EDGE,"E204")}),1.0]])]});
            var Q1;
            Q1=makeQuery(id+"F53.imprint","IMPRINT",FACE,{"disambiguationData":[TD([[makeQuery(id+"F53.imprint","IMPRINT",EDGE,{"derivedFrom":sQuery(id+"F53.wireOp",EDGE,"E205")}),1.0]])]});
            var Q2;
            Q2=makeQuery(id+"F53.imprint","IMPRINT",FACE,{"disambiguationData":[TD([[makeQuery(id+"F53.imprint","IMPRINT",EDGE,{"derivedFrom":sQuery(id+"F53.wireOp",EDGE,"E206")}),1.0]])]});
            var Q3;
            Q3=makeQuery(id+"F53.imprint","IMPRINT",FACE,{"disambiguationData":[TD([[makeQuery(id+"F53.imprint","IMPRINT",EDGE,{"derivedFrom":sQuery(id+"F53.wireOp",EDGE,"E207")}),1.0]])]});
            var Q4;
            Q4=makeQuery(id+"F53.imprint","IMPRINT",FACE,{"disambiguationData":[TD([[makeQuery(id+"F53.imprint","IMPRINT",EDGE,{"derivedFrom":sQuery(id+"F53.wireOp",EDGE,"E208")}),1.0]])]});
            var Q5;
            Q5=makeQuery(id+"F53.imprint","IMPRINT",FACE,{"disambiguationData":[TD([[makeQuery(id+"F53.imprint","IMPRINT",EDGE,{"derivedFrom":sQuery(id+"F53.wireOp",EDGE,"E209")}),1.0]])]});
            var Q6;
            Q6=makeQuery(id+"F53.imprint","IMPRINT",FACE,{"disambiguationData":[TD([[makeQuery(id+"F53.imprint","IMPRINT",EDGE,{"derivedFrom":sQuery(id+"F53.wireOp",EDGE,"E210")}),1.0]])]});
            var Q7;
            Q7=makeQuery(id+"F53.imprint","IMPRINT",FACE,{"disambiguationData":[TD([[makeQuery(id+"F53.imprint","IMPRINT",EDGE,{"derivedFrom":sQuery(id+"F53.wireOp",EDGE,"E211")}),1.0]])]});
            var Q8;
            Q8=makeQuery(id+"F53.imprint","IMPRINT",FACE,{"disambiguationData":[TD([[makeQuery(id+"F53.imprint","IMPRINT",EDGE,{"derivedFrom":sQuery(id+"F53.wireOp",EDGE,"E212")}),1.0]])]});
            var Q9;
            Q9=makeQuery(id+"F53.imprint","IMPRINT",FACE,{"disambiguationData":[TD([[makeQuery(id+"F53.imprint","IMPRINT",EDGE,{"derivedFrom":sQuery(id+"F53.wireOp",EDGE,"E213")}),1.0]])]});
            var Q10;
            Q10=makeQuery(id+"F53.imprint","IMPRINT",FACE,{"disambiguationData":[TD([[makeQuery(id+"F53.imprint","IMPRINT",EDGE,{"derivedFrom":sQuery(id+"F53.wireOp",EDGE,"E214")}),1.0]])]});
            var Q11;
            Q11=makeQuery(id+"F53.imprint","IMPRINT",FACE,{"disambiguationData":[TD([[makeQuery(id+"F53.imprint","IMPRINT",EDGE,{"derivedFrom":sQuery(id+"F53.wireOp",EDGE,"E215")}),1.0]])]});
            extrude(context, id + "F54", {"entities" : qUnion([Q0, Q1, Q2, Q3, Q4, Q5, Q6, Q7, Q8, Q9, Q10, Q11]), "operationType" : NewBodyOperationType.REMOVE, "oppositeDirection" : true, "depth" : 6 * mm});
        }
        {
            var Q0;
            Q0=makeQuery(id+"F23.imprint","IMPRINT",FACE,{"disambiguationData":[TD([[makeQuery(id+"F23.imprint","IMPRINT",EDGE,{"derivedFrom":sQuery(id+"F23.wireOp",EDGE,"E137.bottom")}),-1.0]])]});
            extrude(context, id + "F55", {"entities" : qUnion([Q0]), "depth" : 15 * mm});
        }
        {
            var Q0;
            Q0=makeQuery(id+"F23.imprint","IMPRINT",FACE,{"disambiguationData":[TD([[makeQuery(id+"F23.imprint","IMPRINT",EDGE,{"derivedFrom":sQuery(id+"F23.wireOp",EDGE,"E164")}),-1.0]])]});
            var Q1;
            Q1=makeQuery(id+"F23.imprint","IMPRINT",FACE,{"disambiguationData":[TD([[makeQuery(id+"F23.imprint","IMPRINT",EDGE,{"derivedFrom":sQuery(id+"F23.wireOp",EDGE,"E163")}),-1.0]])]});
            var Q2;
            Q2=makeQuery(id+"F23.imprint","IMPRINT",FACE,{"disambiguationData":[TD([[makeQuery(id+"F23.imprint","IMPRINT",EDGE,{"derivedFrom":sQuery(id+"F23.wireOp",EDGE,"E166")}),-1.0]])]});
            var Q3;
            Q3=makeQuery(id+"F23.imprint","IMPRINT",FACE,{"disambiguationData":[TD([[makeQuery(id+"F23.imprint","IMPRINT",EDGE,{"derivedFrom":sQuery(id+"F23.wireOp",EDGE,"E165")}),-1.0]])]});
            var Q4;
            Q4=makeQuery(id+"F23.imprint","IMPRINT",FACE,{"disambiguationData":[TD([[makeQuery(id+"F23.imprint","IMPRINT",EDGE,{"derivedFrom":sQuery(id+"F23.wireOp",EDGE,"E171.1.0.3")}),-1.0]])]});
            var Q5;
            Q5=makeQuery(id+"F23.imprint","IMPRINT",FACE,{"disambiguationData":[TD([[makeQuery(id+"F23.imprint","IMPRINT",EDGE,{"derivedFrom":sQuery(id+"F23.wireOp",EDGE,"E171.1.0.1")}),-1.0]])]});
            var Q6;
            Q6=makeQuery(id+"F23.imprint","IMPRINT",FACE,{"disambiguationData":[TD([[makeQuery(id+"F23.imprint","IMPRINT",EDGE,{"derivedFrom":sQuery(id+"F23.wireOp",EDGE,"E171.1.0.4")}),1.0]])]});
            var Q7;
            Q7=makeQuery(id+"F23.imprint","IMPRINT",FACE,{"disambiguationData":[TD([[makeQuery(id+"F23.imprint","IMPRINT",EDGE,{"derivedFrom":sQuery(id+"F23.wireOp",EDGE,"E171.1.0.0")}),-1.0]])]});
            var Q8;
            Q8=makeQuery(id+"F23.imprint","IMPRINT",FACE,{"disambiguationData":[TD([[makeQuery(id+"F23.imprint","IMPRINT",EDGE,{"derivedFrom":sQuery(id+"F23.wireOp",EDGE,"E172.1.0.3")}),1.0]])]});
            var Q9;
            Q9=makeQuery(id+"F23.imprint","IMPRINT",FACE,{"disambiguationData":[TD([[makeQuery(id+"F23.imprint","IMPRINT",EDGE,{"derivedFrom":sQuery(id+"F23.wireOp",EDGE,"E172.1.0.12")}),1.0]])]});
            var Q10;
            Q10=makeQuery(id+"F23.imprint","IMPRINT",FACE,{"disambiguationData":[TD([[makeQuery(id+"F23.imprint","IMPRINT",EDGE,{"derivedFrom":sQuery(id+"F23.wireOp",EDGE,"E172.1.0.11")}),1.0]])]});
            var Q11;
            Q11=makeQuery(id+"F23.imprint","IMPRINT",FACE,{"disambiguationData":[TD([[makeQuery(id+"F23.imprint","IMPRINT",EDGE,{"derivedFrom":sQuery(id+"F23.wireOp",EDGE,"E172.1.0.4")}),1.0]])]});
            var Q12;
            Q12=makeQuery(id+"F23.imprint","IMPRINT",FACE,{"disambiguationData":[TD([[makeQuery(id+"F23.imprint","IMPRINT",EDGE,{"derivedFrom":sQuery(id+"F23.wireOp",EDGE,"E172.1.0.2")}),-1.0]])]});
            var Q13;
            Q13=makeQuery(id+"F23.imprint","IMPRINT",FACE,{"disambiguationData":[TD([[makeQuery(id+"F23.imprint","IMPRINT",EDGE,{"derivedFrom":sQuery(id+"F23.wireOp",EDGE,"E172.1.0.1")}),-1.0]])]});
            var Q14;
            Q14=makeQuery(id+"F23.imprint","IMPRINT",FACE,{"disambiguationData":[TD([[makeQuery(id+"F23.imprint","IMPRINT",EDGE,{"derivedFrom":sQuery(id+"F23.wireOp",EDGE,"E172.1.0.14")}),-1.0]])]});
            var Q15;
            Q15=makeQuery(id+"F23.imprint","IMPRINT",FACE,{"disambiguationData":[TD([[makeQuery(id+"F23.imprint","IMPRINT",EDGE,{"derivedFrom":sQuery(id+"F23.wireOp",EDGE,"E172.1.0.6")}),1.0]])]});
            var Q16;
            Q16=sQuery(id+"F23.wireOp",EDGE,"E167");
            extrude(context, id + "F56", {"entities" : qUnion([Q0, Q1, Q2, Q3, Q4, Q5, Q6, Q7, Q8, Q9, Q10, Q11, Q12, Q13, Q14, Q15]), "operationType" : NewBodyOperationType.ADD, "surfaceEntities" : qUnion([Q16]), "depth" : 15 * mm});
        }
        {
            var Q0;
            Q0=makeQuery(id+"F23.imprint","IMPRINT",FACE,{"disambiguationData":[TD([[makeQuery(id+"F23.imprint","IMPRINT",EDGE,{"derivedFrom":sQuery(id+"F23.wireOp",EDGE,"E164")}),-1.0]])]});
            var Q1;
            Q1=makeQuery(id+"F23.imprint","IMPRINT",FACE,{"disambiguationData":[TD([[makeQuery(id+"F23.imprint","IMPRINT",EDGE,{"derivedFrom":sQuery(id+"F23.wireOp",EDGE,"E163")}),-1.0]])]});
            var Q2;
            Q2=makeQuery(id+"F23.imprint","IMPRINT",FACE,{"disambiguationData":[TD([[makeQuery(id+"F23.imprint","IMPRINT",EDGE,{"derivedFrom":sQuery(id+"F23.wireOp",EDGE,"E166")}),-1.0]])]});
            var Q3;
            Q3=makeQuery(id+"F23.imprint","IMPRINT",FACE,{"disambiguationData":[TD([[makeQuery(id+"F23.imprint","IMPRINT",EDGE,{"derivedFrom":sQuery(id+"F23.wireOp",EDGE,"E165")}),-1.0]])]});
            var Q4;
            Q4=makeQuery(id+"F23.imprint","IMPRINT",FACE,{"disambiguationData":[TD([[makeQuery(id+"F23.imprint","IMPRINT",EDGE,{"derivedFrom":sQuery(id+"F23.wireOp",EDGE,"E171.1.0.3")}),-1.0]])]});
            var Q5;
            Q5=makeQuery(id+"F23.imprint","IMPRINT",FACE,{"disambiguationData":[TD([[makeQuery(id+"F23.imprint","IMPRINT",EDGE,{"derivedFrom":sQuery(id+"F23.wireOp",EDGE,"E171.1.0.1")}),-1.0]])]});
            var Q6;
            Q6=makeQuery(id+"F23.imprint","IMPRINT",FACE,{"disambiguationData":[TD([[makeQuery(id+"F23.imprint","IMPRINT",EDGE,{"derivedFrom":sQuery(id+"F23.wireOp",EDGE,"E171.1.0.4")}),1.0]])]});
            var Q7;
            Q7=makeQuery(id+"F23.imprint","IMPRINT",FACE,{"disambiguationData":[TD([[makeQuery(id+"F23.imprint","IMPRINT",EDGE,{"derivedFrom":sQuery(id+"F23.wireOp",EDGE,"E171.1.0.0")}),-1.0]])]});
            var Q8;
            Q8=makeQuery(id+"F23.imprint","IMPRINT",FACE,{"disambiguationData":[TD([[makeQuery(id+"F23.imprint","IMPRINT",EDGE,{"derivedFrom":sQuery(id+"F23.wireOp",EDGE,"E172.1.0.3")}),1.0]])]});
            var Q9;
            Q9=makeQuery(id+"F23.imprint","IMPRINT",FACE,{"disambiguationData":[TD([[makeQuery(id+"F23.imprint","IMPRINT",EDGE,{"derivedFrom":sQuery(id+"F23.wireOp",EDGE,"E172.1.0.12")}),1.0]])]});
            var Q10;
            Q10=makeQuery(id+"F23.imprint","IMPRINT",FACE,{"disambiguationData":[TD([[makeQuery(id+"F23.imprint","IMPRINT",EDGE,{"derivedFrom":sQuery(id+"F23.wireOp",EDGE,"E172.1.0.11")}),1.0]])]});
            var Q11;
            Q11=makeQuery(id+"F23.imprint","IMPRINT",FACE,{"disambiguationData":[TD([[makeQuery(id+"F23.imprint","IMPRINT",EDGE,{"derivedFrom":sQuery(id+"F23.wireOp",EDGE,"E172.1.0.4")}),1.0]])]});
            var Q12;
            Q12=makeQuery(id+"F23.imprint","IMPRINT",FACE,{"disambiguationData":[TD([[makeQuery(id+"F23.imprint","IMPRINT",EDGE,{"derivedFrom":sQuery(id+"F23.wireOp",EDGE,"E172.1.0.2")}),-1.0]])]});
            var Q13;
            Q13=makeQuery(id+"F23.imprint","IMPRINT",FACE,{"disambiguationData":[TD([[makeQuery(id+"F23.imprint","IMPRINT",EDGE,{"derivedFrom":sQuery(id+"F23.wireOp",EDGE,"E172.1.0.1")}),-1.0]])]});
            var Q14;
            Q14=makeQuery(id+"F23.imprint","IMPRINT",FACE,{"disambiguationData":[TD([[makeQuery(id+"F23.imprint","IMPRINT",EDGE,{"derivedFrom":sQuery(id+"F23.wireOp",EDGE,"E172.1.0.14")}),-1.0]])]});
            var Q15;
            Q15=makeQuery(id+"F23.imprint","IMPRINT",FACE,{"disambiguationData":[TD([[makeQuery(id+"F23.imprint","IMPRINT",EDGE,{"derivedFrom":sQuery(id+"F23.wireOp",EDGE,"E172.1.0.6")}),1.0]])]});
            extrude(context, id + "F57", {"entities" : qUnion([Q0, Q1, Q2, Q3, Q4, Q5, Q6, Q7, Q8, Q9, Q10, Q11, Q12, Q13, Q14, Q15]), "operationType" : NewBodyOperationType.REMOVE, "depth" : 6 * mm});
        }
    });
